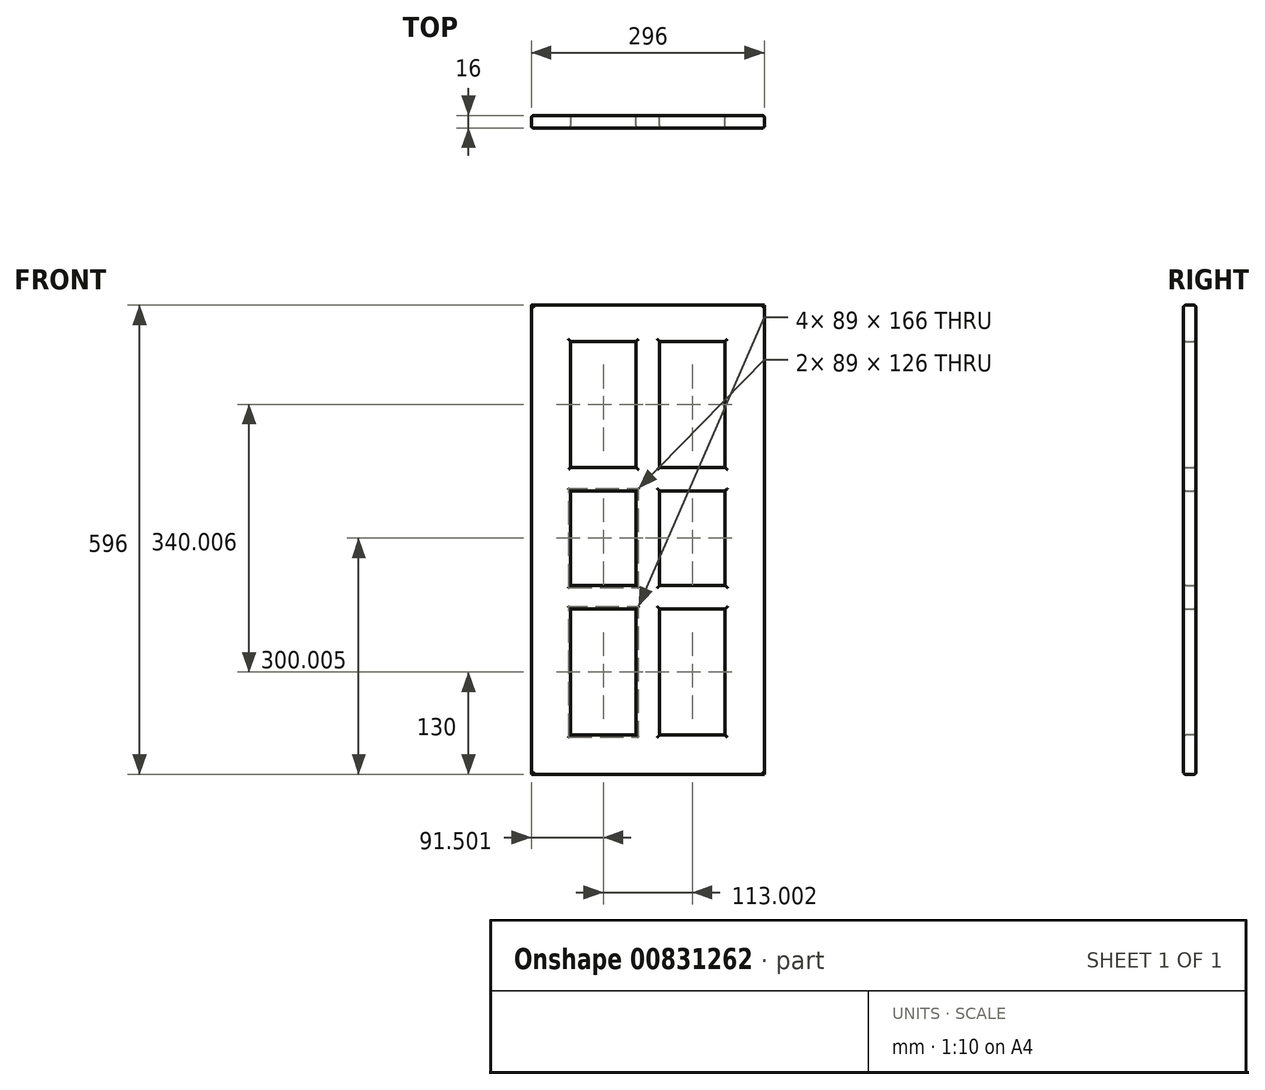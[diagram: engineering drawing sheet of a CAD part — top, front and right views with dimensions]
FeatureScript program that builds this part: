
annotation { "Feature Type Name" : "Feature", "Feature Type Description" : "" }
export const myFeature = defineFeature(function(context is Context, id is Id, definition is map)
    precondition{}
    {
        {
            var Q0;
            Q0=qCreatedBy(makeId("Front.planeOp"),FACE);
            var sketch = newSketch(context, id + "F0", { "sketchPlane" : qUnion([Q0])});
            skLineSegment(sketch, "E0.bottom", {"start": v(0, 0) * mm, "end": v(28.85, 0) * mm});
            skLineSegment(sketch, "E0.top", {"start": v(0, 37.88) * mm, "end": v(28.85, 37.88) * mm});
            skLineSegment(sketch, "E0.left", {"start": v(0, 0) * mm, "end": v(0, 37.88) * mm});
            skLineSegment(sketch, "E0.right", {"start": v(28.85, 0) * mm, "end": v(28.85, 37.88) * mm});
            skSolve(sketch);
        }
        {
            var Q0;
            Q0=makeQuery(id+"F0.imprint","IMPRINT",FACE,{"disambiguationData":[TD([[makeQuery(id+"F0.imprint","IMPRINT",EDGE,{"derivedFrom":sQuery(id+"F0.wireOp",EDGE,"E0.bottom")}),1.0]])]});
            extrude(context, id + "F1", {"entities" : qUnion([Q0]), "depth" : 16 * mm, "offsetDistance" : 25.4 * mm});
        }
        {
            var Q0;
            Q0=makeQuery(id+"F1.opExtrude","SWEPT_FACE",FACE,{"disambiguationData":[OSD([sQuery(id+"F0.wireOp",EDGE,"E0.left")])]});
            extrude(context, id + "F2", {"entities" : qUnion([Q0]), "operationType" : NewBodyOperationType.ADD, "oppositeDirection" : true, "depth" : 296 * mm, "offsetDistance" : 25.4 * mm});
        }
        {
            var Q0;
            {var subQ0=sQuery(id+"F0.wireOp",EDGE,"E0.bottom");Q0=makeQuery(id+"F2.boolean.opBoolean","MERGE",FACE,{"derivedFrom":[makeQuery(id+"F1.opExtrude","SWEPT_FACE",FACE,{"disambiguationData":[OSD([subQ0])]}),makeQuery(id+"F2.opExtrude","SWEPT_FACE",FACE,{"disambiguationData":[OSD([subQ0,sQuery(id+"F0.wireOp",EDGE,"E0.left")])]})]});}
            extrude(context, id + "F3", {"entities" : qUnion([Q0]), "operationType" : NewBodyOperationType.ADD, "oppositeDirection" : true, "depth" : 996 * mm, "offsetDistance" : 25 * mm});
        }
        {
            var Q0;
            {var subQ0=sQuery(id+"F0.wireOp",EDGE,"E0.left");var subQ1=sQuery(id+"F0.wireOp",EDGE,"E0.bottom");Q0=makeQuery(id+"F3.boolean.opBoolean","MERGE",FACE,{"derivedFrom":[makeQuery(id+"F2.boolean.opBoolean","MERGE",FACE,{"derivedFrom":[makeQuery(id+"F1.opExtrude","CAP_FACE",FACE,{"disambiguationData":[OSD([subQ1,sQuery(id+"F0.wireOp",EDGE,"E0.top"),subQ0,sQuery(id+"F0.wireOp",EDGE,"E0.right")])],"isStart":false}),makeQuery(id+"F2.opExtrude","SWEPT_FACE",FACE,{"disambiguationData":[OSD([subQ0]),TDD([makeQuery(id+"F1.opExtrude","CAP_EDGE",EDGE,{"disambiguationData":[OSD([subQ0])],"isStart":false})])]})]}),makeQuery(id+"F3.opExtrude","SWEPT_FACE",FACE,{"disambiguationData":[OSD([subQ1,subQ0]),TDD([makeQuery(id+"F2.boolean.opBoolean","MERGE",EDGE,{"derivedFrom":[makeQuery(id+"F1.opExtrude","CAP_EDGE",EDGE,{"disambiguationData":[OSD([subQ1])],"isStart":false}),makeQuery(id+"F2.opExtrude","SWEPT_EDGE",EDGE,{"disambiguationData":[OSD([subQ1,subQ0]),TDD([makeQuery(id+"F1.opExtrude","CAP_VERTEX",VERTEX,{"disambiguationData":[OSD([subQ1,subQ0])],"isStart":false})])]})]})])]})]});}
            var sketch = newSketch(context, id + "F4", { "sketchPlane" : qUnion([Q0])});
            skLineSegment(sketch, "E1.bottom", {"start": v(48.4, 906.79) * mm, "end": v(248.24, 906.79) * mm});
            skLineSegment(sketch, "E1.top", {"start": v(48.4, 105.66) * mm, "end": v(248.24, 105.66) * mm});
            skLineSegment(sketch, "E1.left", {"start": v(48.4, 906.79) * mm, "end": v(48.4, 105.66) * mm});
            skLineSegment(sketch, "E1.right", {"start": v(248.24, 906.79) * mm, "end": v(248.24, 105.66) * mm});
            skSolve(sketch);
        }
        {
            var Q0;
            Q0=makeQuery(id+"F4.imprint","IMPRINT",FACE,{"disambiguationData":[TD([[makeQuery(id+"F4.imprint","IMPRINT",EDGE,{"derivedFrom":sQuery(id+"F4.wireOp",EDGE,"E1.bottom")}),-1.0]])]});
            extrude(context, id + "F5", {"entities" : qUnion([Q0]), "operationType" : NewBodyOperationType.REMOVE, "oppositeDirection" : true, "depth" : 5 * mm, "offsetDistance" : 25 * mm});
        }
        {
            var Q0;
            Q0=makeQuery(id+"F5.boolean.opBoolean","COPY",FACE,{"derivedFrom":makeQuery(id+"F5.opExtrude","SWEPT_FACE",FACE,{"disambiguationData":[OSD([sQuery(id+"F4.wireOp",EDGE,"E1.bottom")])]})});
            extrude(context, id + "F6", {"entities" : qUnion([Q0]), "operationType" : NewBodyOperationType.REMOVE, "oppositeDirection" : true, "depth" : 39.2 * mm, "offsetDistance" : 25 * mm});
        }
        {
            var Q0;
            {var subQ0=sQuery(id+"F4.wireOp",EDGE,"E1.right");Q0=makeQuery(id+"F6.boolean.opBoolean","MERGE",FACE,{"derivedFrom":[makeQuery(id+"F5.boolean.opBoolean","COPY",FACE,{"derivedFrom":makeQuery(id+"F5.opExtrude","SWEPT_FACE",FACE,{"disambiguationData":[OSD([subQ0])]})}),makeQuery(id+"F6.opExtrude","SWEPT_FACE",FACE,{"disambiguationData":[OSD([sQuery(id+"F4.wireOp",EDGE,"E1.bottom"),subQ0])]})]});}
            extrude(context, id + "F7", {"entities" : qUnion([Q0]), "operationType" : NewBodyOperationType.ADD, "depth" : 2.24 * mm, "offsetDistance" : 25 * mm});
        }
        {
            var Q0;
            Q0=makeQuery(id+"F5.boolean.opBoolean","COPY",FACE,{"derivedFrom":makeQuery(id+"F5.opExtrude","SWEPT_FACE",FACE,{"disambiguationData":[OSD([sQuery(id+"F4.wireOp",EDGE,"E1.top")])]})});
            extrude(context, id + "F8", {"entities" : qUnion([Q0]), "operationType" : NewBodyOperationType.REMOVE, "oppositeDirection" : true, "depth" : 55.66 * mm, "offsetDistance" : 25 * mm});
        }
        {
            var Q0;
            {var subQ0=sQuery(id+"F4.wireOp",EDGE,"E1.left");Q0=makeQuery(id+"F8.boolean.opBoolean","MERGE",FACE,{"derivedFrom":[makeQuery(id+"F6.boolean.opBoolean","MERGE",FACE,{"derivedFrom":[makeQuery(id+"F5.boolean.opBoolean","COPY",FACE,{"derivedFrom":makeQuery(id+"F5.opExtrude","SWEPT_FACE",FACE,{"disambiguationData":[OSD([subQ0])]})}),makeQuery(id+"F6.opExtrude","SWEPT_FACE",FACE,{"disambiguationData":[OSD([sQuery(id+"F4.wireOp",EDGE,"E1.bottom"),subQ0])]})]}),makeQuery(id+"F8.opExtrude","SWEPT_FACE",FACE,{"disambiguationData":[OSD([sQuery(id+"F4.wireOp",EDGE,"E1.top"),subQ0])]})]});}
            extrude(context, id + "F9", {"entities" : qUnion([Q0]), "operationType" : NewBodyOperationType.ADD, "depth" : 1.59 * mm, "offsetDistance" : 25 * mm});
        }
        {
            var Q0;
            {var subQ0=sQuery(id+"F4.wireOp",EDGE,"E1.top");var subQ1=sQuery(id+"F4.wireOp",EDGE,"E1.bottom");Q0=makeQuery(id+"F8.boolean.opBoolean","MERGE",FACE,{"derivedFrom":[makeQuery(id+"F6.boolean.opBoolean","MERGE",FACE,{"derivedFrom":[makeQuery(id+"F5.boolean.opBoolean","COPY",FACE,{"derivedFrom":makeQuery(id+"F5.opExtrude","CAP_FACE",FACE,{"disambiguationData":[OSD([subQ1,subQ0,sQuery(id+"F4.wireOp",EDGE,"E1.left"),sQuery(id+"F4.wireOp",EDGE,"E1.right")])],"isStart":false})}),makeQuery(id+"F6.opExtrude","SWEPT_FACE",FACE,{"disambiguationData":[OSD([subQ1]),TDD([makeQuery(id+"F5.boolean.opBoolean","COPY",EDGE,{"derivedFrom":makeQuery(id+"F5.opExtrude","CAP_EDGE",EDGE,{"disambiguationData":[OSD([subQ1])],"isStart":false})})])]})]}),makeQuery(id+"F8.opExtrude","SWEPT_FACE",FACE,{"disambiguationData":[OSD([subQ0]),TDD([makeQuery(id+"F5.boolean.opBoolean","COPY",EDGE,{"derivedFrom":makeQuery(id+"F5.opExtrude","CAP_EDGE",EDGE,{"disambiguationData":[OSD([subQ0])],"isStart":false})})])]})]});}
            var sketch = newSketch(context, id + "F10", { "sketchPlane" : qUnion([Q0])});
            skLineSegment(sketch, "E2.bottom", {"start": v(127.14, 946) * mm, "end": v(181.91, 946) * mm});
            skLineSegment(sketch, "E2.top", {"start": v(127.14, 50) * mm, "end": v(181.91, 50) * mm});
            skLineSegment(sketch, "E2.left", {"start": v(127.14, 946) * mm, "end": v(127.14, 50) * mm});
            skLineSegment(sketch, "E2.right", {"start": v(181.91, 946) * mm, "end": v(181.91, 50) * mm});
            skSolve(sketch);
        }
        {
            var Q0;
            Q0=makeQuery(id+"F10.imprint","IMPRINT",FACE,{"disambiguationData":[TD([[makeQuery(id+"F10.imprint","IMPRINT",EDGE,{"derivedFrom":sQuery(id+"F10.wireOp",EDGE,"E2.bottom")}),-1.0]])]});
            extrude(context, id + "F11", {"entities" : qUnion([Q0]), "operationType" : NewBodyOperationType.ADD, "depth" : 5 * mm, "offsetDistance" : 25 * mm});
        }
        {
            var Q0;
            Q0=makeQuery(id+"F11.opExtrude","SWEPT_FACE",FACE,{"disambiguationData":[OSD([sQuery(id+"F10.wireOp",EDGE,"E2.left")])]});
            extrude(context, id + "F12", {"entities" : qUnion([Q0]), "operationType" : NewBodyOperationType.REMOVE, "oppositeDirection" : true, "depth" : 5.86 * mm, "offsetDistance" : 25 * mm});
        }
        {
            var Q0;
            Q0=makeQuery(id+"F11.opExtrude","SWEPT_FACE",FACE,{"disambiguationData":[OSD([sQuery(id+"F10.wireOp",EDGE,"E2.right")])]});
            extrude(context, id + "F13", {"entities" : qUnion([Q0]), "operationType" : NewBodyOperationType.REMOVE, "oppositeDirection" : true, "depth" : 18.91 * mm, "offsetDistance" : 25 * mm});
        }
        {
            var Q0;
            {var subQ0=sQuery(id+"F10.wireOp",EDGE,"E2.left");var subQ1=sQuery(id+"F4.wireOp",EDGE,"E1.bottom");var subQ2=sQuery(id+"F4.wireOp",EDGE,"E1.top");var subQ3=sQuery(id+"F4.wireOp",EDGE,"E1.left");Q0=makeQuery(id+"F12.boolean.opBoolean","MERGE",FACE,{"derivedFrom":[makeQuery(id+"F11.boolean.opBoolean","SPLIT",FACE,{"disambiguationData":[TD([makeQuery(id+"F11.opExtrude","SWEPT_FACE",FACE,{"disambiguationData":[OSD([subQ0])]})])],"derivedFrom":makeQuery(id+"F8.boolean.opBoolean","MERGE",FACE,{"derivedFrom":[makeQuery(id+"F6.boolean.opBoolean","MERGE",FACE,{"derivedFrom":[makeQuery(id+"F5.boolean.opBoolean","COPY",FACE,{"derivedFrom":makeQuery(id+"F5.opExtrude","CAP_FACE",FACE,{"disambiguationData":[OSD([subQ1,subQ2,subQ3,sQuery(id+"F4.wireOp",EDGE,"E1.right")])],"isStart":false})}),makeQuery(id+"F6.opExtrude","SWEPT_FACE",FACE,{"disambiguationData":[OSD([subQ1]),TDD([makeQuery(id+"F5.boolean.opBoolean","COPY",EDGE,{"derivedFrom":makeQuery(id+"F5.opExtrude","CAP_EDGE",EDGE,{"disambiguationData":[OSD([subQ1])],"isStart":false})})])]})]}),makeQuery(id+"F8.opExtrude","SWEPT_FACE",FACE,{"disambiguationData":[OSD([subQ2]),TDD([makeQuery(id+"F5.boolean.opBoolean","COPY",EDGE,{"derivedFrom":makeQuery(id+"F5.opExtrude","CAP_EDGE",EDGE,{"disambiguationData":[OSD([subQ2])],"isStart":false})})])]})]})}),makeQuery(id+"F12.opExtrude","SWEPT_FACE",FACE,{"disambiguationData":[OSD([subQ0]),TDD([makeQuery(id+"F11.opExtrude","CAP_EDGE",EDGE,{"disambiguationData":[OSD([subQ0])],"isStart":true})])]})]});}
            var sketch = newSketch(context, id + "F14", { "sketchPlane" : qUnion([Q0])});
            skLineSegment(sketch, "E3.bottom", {"start": v(50, 870.78) * mm, "end": v(133, 870.78) * mm});
            skLineSegment(sketch, "E3.top", {"start": v(50, 835.83) * mm, "end": v(133, 835.83) * mm});
            skLineSegment(sketch, "E3.left", {"start": v(50, 870.78) * mm, "end": v(50, 835.83) * mm});
            skLineSegment(sketch, "E3.right", {"start": v(133, 870.78) * mm, "end": v(133, 835.83) * mm});
            skLineSegment(sketch, "E4.bottom", {"start": v(50, 539.3) * mm, "end": v(133, 539.3) * mm});
            skLineSegment(sketch, "E4.top", {"start": v(50, 484.02) * mm, "end": v(133, 484.02) * mm});
            skLineSegment(sketch, "E4.left", {"start": v(50, 539.3) * mm, "end": v(50, 484.02) * mm});
            skLineSegment(sketch, "E4.right", {"start": v(133, 539.3) * mm, "end": v(133, 484.02) * mm});
            skSolve(sketch);
        }
        {
            var Q0;
            {var subQ0=sQuery(id+"F10.wireOp",EDGE,"E2.right");var subQ1=sQuery(id+"F4.wireOp",EDGE,"E1.top");var subQ2=sQuery(id+"F4.wireOp",EDGE,"E1.right");var subQ3=sQuery(id+"F4.wireOp",EDGE,"E1.bottom");Q0=makeQuery(id+"F13.boolean.opBoolean","MERGE",FACE,{"derivedFrom":[makeQuery(id+"F11.boolean.opBoolean","SPLIT",FACE,{"disambiguationData":[TD([makeQuery(id+"F11.opExtrude","SWEPT_FACE",FACE,{"disambiguationData":[OSD([subQ0])]})])],"derivedFrom":makeQuery(id+"F8.boolean.opBoolean","MERGE",FACE,{"derivedFrom":[makeQuery(id+"F6.boolean.opBoolean","MERGE",FACE,{"derivedFrom":[makeQuery(id+"F5.boolean.opBoolean","COPY",FACE,{"derivedFrom":makeQuery(id+"F5.opExtrude","CAP_FACE",FACE,{"disambiguationData":[OSD([subQ3,subQ1,sQuery(id+"F4.wireOp",EDGE,"E1.left"),subQ2])],"isStart":false})}),makeQuery(id+"F6.opExtrude","SWEPT_FACE",FACE,{"disambiguationData":[OSD([subQ3]),TDD([makeQuery(id+"F5.boolean.opBoolean","COPY",EDGE,{"derivedFrom":makeQuery(id+"F5.opExtrude","CAP_EDGE",EDGE,{"disambiguationData":[OSD([subQ3])],"isStart":false})})])]})]}),makeQuery(id+"F8.opExtrude","SWEPT_FACE",FACE,{"disambiguationData":[OSD([subQ1]),TDD([makeQuery(id+"F5.boolean.opBoolean","COPY",EDGE,{"derivedFrom":makeQuery(id+"F5.opExtrude","CAP_EDGE",EDGE,{"disambiguationData":[OSD([subQ1])],"isStart":false})})])]})]})}),makeQuery(id+"F13.opExtrude","SWEPT_FACE",FACE,{"disambiguationData":[OSD([subQ0]),TDD([makeQuery(id+"F11.opExtrude","CAP_EDGE",EDGE,{"disambiguationData":[OSD([subQ0])],"isStart":true})])]})]});}
            var sketch = newSketch(context, id + "F15", { "sketchPlane" : qUnion([Q0])});
            skLineSegment(sketch, "E5.bottom", {"start": v(163, 876.14) * mm, "end": v(246, 876.14) * mm});
            skLineSegment(sketch, "E5.top", {"start": v(163, 831.26) * mm, "end": v(246, 831.26) * mm});
            skLineSegment(sketch, "E5.left", {"start": v(163, 876.14) * mm, "end": v(163, 831.26) * mm});
            skLineSegment(sketch, "E5.right", {"start": v(246, 876.14) * mm, "end": v(246, 831.26) * mm});
            skLineSegment(sketch, "E6.bottom", {"start": v(163, 602.8) * mm, "end": v(246, 602.8) * mm});
            skLineSegment(sketch, "E6.top", {"start": v(163, 550.28) * mm, "end": v(246, 550.28) * mm});
            skLineSegment(sketch, "E6.left", {"start": v(163, 602.8) * mm, "end": v(163, 550.28) * mm});
            skLineSegment(sketch, "E6.right", {"start": v(246, 602.8) * mm, "end": v(246, 550.28) * mm});
            skSolve(sketch);
        }
        {
            var Q0;
            Q0=makeQuery(id+"F14.imprint","IMPRINT",FACE,{"disambiguationData":[TD([[makeQuery(id+"F14.imprint","IMPRINT",EDGE,{"derivedFrom":sQuery(id+"F14.wireOp",EDGE,"E3.bottom")}),-1.0]])]});
            var Q1;
            Q1=makeQuery(id+"F15.imprint","IMPRINT",FACE,{"disambiguationData":[TD([[makeQuery(id+"F15.imprint","IMPRINT",EDGE,{"derivedFrom":sQuery(id+"F15.wireOp",EDGE,"E5.bottom")}),-1.0]])]});
            var Q2;
            Q2=makeQuery(id+"F15.imprint","IMPRINT",FACE,{"disambiguationData":[TD([[makeQuery(id+"F15.imprint","IMPRINT",EDGE,{"derivedFrom":sQuery(id+"F15.wireOp",EDGE,"E6.bottom")}),-1.0]])]});
            var Q3;
            Q3=makeQuery(id+"F14.imprint","IMPRINT",FACE,{"disambiguationData":[TD([[makeQuery(id+"F14.imprint","IMPRINT",EDGE,{"derivedFrom":sQuery(id+"F14.wireOp",EDGE,"E4.bottom")}),-1.0]])]});
            extrude(context, id + "F16", {"entities" : qUnion([Q0, Q1, Q2, Q3]), "operationType" : NewBodyOperationType.ADD, "depth" : 5 * mm, "offsetDistance" : 25 * mm});
        }
        {
            var Q0;
            Q0=makeQuery(id+"F16.opExtrude","SWEPT_FACE",FACE,{"disambiguationData":[OSD([sQuery(id+"F15.wireOp",EDGE,"E6.top")])]});
            var Q1;
            Q1=makeQuery(id+"F16.opExtrude","SWEPT_FACE",FACE,{"disambiguationData":[OSD([sQuery(id+"F14.wireOp",EDGE,"E4.top")])]});
            extrude(context, id + "F17", {"entities" : qUnion([Q0, Q1]), "operationType" : NewBodyOperationType.ADD, "depth" : 300 * mm, "offsetDistance" : 25 * mm});
        }
        {
            var Q0;
            Q0=makeQuery(id+"F16.opExtrude","SWEPT_FACE",FACE,{"disambiguationData":[OSD([sQuery(id+"F14.wireOp",EDGE,"E4.bottom")])]});
            var Q1;
            Q1=makeQuery(id+"F16.opExtrude","SWEPT_FACE",FACE,{"disambiguationData":[OSD([sQuery(id+"F15.wireOp",EDGE,"E6.bottom")])]});
            extrude(context, id + "F18", {"entities" : qUnion([Q0, Q1]), "operationType" : NewBodyOperationType.REMOVE, "oppositeDirection" : true, "depth" : 300 * mm, "offsetDistance" : 25 * mm});
        }
        {
            var Q0;
            Q0=makeQuery(id+"F16.opExtrude","SWEPT_FACE",FACE,{"disambiguationData":[OSD([sQuery(id+"F14.wireOp",EDGE,"E3.top")])]});
            extrude(context, id + "F19", {"entities" : qUnion([Q0]), "operationType" : NewBodyOperationType.ADD, "depth" : 324.8 * mm, "offsetDistance" : 25 * mm});
        }
        {
            var Q0;
            Q0=makeQuery(id+"F16.opExtrude","SWEPT_FACE",FACE,{"disambiguationData":[OSD([sQuery(id+"F14.wireOp",EDGE,"E3.bottom")])]});
            extrude(context, id + "F20", {"entities" : qUnion([Q0]), "operationType" : NewBodyOperationType.REMOVE, "oppositeDirection" : true, "depth" : 324.8 * mm, "offsetDistance" : 25 * mm});
        }
        {
            var Q0;
            Q0=makeQuery(id+"F18.boolean.opBoolean","COPY",FACE,{"derivedFrom":makeQuery(id+"F18.opExtrude","CAP_FACE",FACE,{"disambiguationData":[OSD([sQuery(id+"F14.wireOp",EDGE,"E4.bottom")])],"isStart":false})});
            extrude(context, id + "F21", {"entities" : qUnion([Q0]), "operationType" : NewBodyOperationType.ADD, "depth" : 250 * mm, "offsetDistance" : 25 * mm});
        }
        {
            var Q0;
            Q0=makeQuery(id+"F17.opExtrude","CAP_FACE",FACE,{"disambiguationData":[OSD([sQuery(id+"F14.wireOp",EDGE,"E4.top")])],"isStart":false});
            extrude(context, id + "F22", {"entities" : qUnion([Q0]), "operationType" : NewBodyOperationType.REMOVE, "oppositeDirection" : true, "depth" : 250 * mm, "offsetDistance" : 25 * mm});
        }
        {
            var Q0;
            Q0=makeQuery(id+"F20.boolean.opBoolean","COPY",FACE,{"derivedFrom":makeQuery(id+"F20.opExtrude","CAP_FACE",FACE,{"disambiguationData":[OSD([sQuery(id+"F14.wireOp",EDGE,"E3.bottom")])],"isStart":false})});
            extrude(context, id + "F23", {"entities" : qUnion([Q0]), "operationType" : NewBodyOperationType.ADD, "depth" : 100 * mm, "offsetDistance" : 25 * mm});
        }
        {
            var Q0;
            Q0=makeQuery(id+"F19.opExtrude","CAP_FACE",FACE,{"disambiguationData":[OSD([sQuery(id+"F14.wireOp",EDGE,"E3.top")])],"isStart":false});
            extrude(context, id + "F24", {"entities" : qUnion([Q0]), "operationType" : NewBodyOperationType.REMOVE, "oppositeDirection" : true, "depth" : 100 * mm, "offsetDistance" : 25 * mm});
        }
        {
            var Q0;
            Q0=makeQuery(id+"F23.opExtrude","CAP_FACE",FACE,{"disambiguationData":[OSD([sQuery(id+"F14.wireOp",EDGE,"E3.bottom")])],"isStart":false});
            extrude(context, id + "F25", {"entities" : qUnion([Q0]), "operationType" : NewBodyOperationType.ADD, "depth" : 50 * mm, "offsetDistance" : 25 * mm});
        }
        {
            var Q0;
            Q0=makeQuery(id+"F24.boolean.opBoolean","COPY",FACE,{"derivedFrom":makeQuery(id+"F24.opExtrude","CAP_FACE",FACE,{"disambiguationData":[OSD([sQuery(id+"F14.wireOp",EDGE,"E3.top")])],"isStart":false})});
            extrude(context, id + "F26", {"entities" : qUnion([Q0]), "operationType" : NewBodyOperationType.REMOVE, "oppositeDirection" : true, "depth" : 50 * mm, "offsetDistance" : 25 * mm});
        }
        {
            var Q0;
            Q0=makeQuery(id+"F22.boolean.opBoolean","COPY",FACE,{"derivedFrom":makeQuery(id+"F22.opExtrude","CAP_FACE",FACE,{"disambiguationData":[OSD([sQuery(id+"F14.wireOp",EDGE,"E4.top")])],"isStart":false})});
            extrude(context, id + "F27", {"entities" : qUnion([Q0]), "operationType" : NewBodyOperationType.ADD, "depth" : 134.02 * mm, "offsetDistance" : 25 * mm});
        }
        {
            var Q0;
            Q0=makeQuery(id+"F27.opExtrude","CAP_FACE",FACE,{"disambiguationData":[OSD([sQuery(id+"F14.wireOp",EDGE,"E4.top")])],"isStart":false});
            extrude(context, id + "F28", {"entities" : qUnion([Q0]), "operationType" : NewBodyOperationType.REMOVE, "oppositeDirection" : true, "depth" : 100 * mm, "offsetDistance" : 25 * mm});
        }
        {
            var Q0;
            Q0=makeQuery(id+"F26.boolean.opBoolean","COPY",FACE,{"derivedFrom":makeQuery(id+"F26.opExtrude","CAP_FACE",FACE,{"disambiguationData":[OSD([sQuery(id+"F14.wireOp",EDGE,"E3.top")])],"isStart":false})});
            extrude(context, id + "F29", {"entities" : qUnion([Q0]), "operationType" : NewBodyOperationType.ADD, "depth" : 100 * mm, "offsetDistance" : 25 * mm});
        }
        {
            var Q0;
            Q0=makeQuery(id+"F25.opExtrude","CAP_FACE",FACE,{"disambiguationData":[OSD([sQuery(id+"F14.wireOp",EDGE,"E3.bottom")])],"isStart":false});
            extrude(context, id + "F30", {"entities" : qUnion([Q0]), "operationType" : NewBodyOperationType.REMOVE, "oppositeDirection" : true, "depth" : 100 * mm, "offsetDistance" : 25 * mm});
        }
        {
            var Q0;
            Q0=makeQuery(id+"F30.boolean.opBoolean","COPY",FACE,{"derivedFrom":makeQuery(id+"F30.opExtrude","CAP_FACE",FACE,{"disambiguationData":[OSD([sQuery(id+"F14.wireOp",EDGE,"E3.bottom")])],"isStart":false})});
            extrude(context, id + "F31", {"entities" : qUnion([Q0]), "operationType" : NewBodyOperationType.ADD, "depth" : 50 * mm, "offsetDistance" : 25 * mm});
        }
        {
            var Q0;
            Q0=makeQuery(id+"F29.opExtrude","CAP_FACE",FACE,{"disambiguationData":[OSD([sQuery(id+"F14.wireOp",EDGE,"E3.top")])],"isStart":false});
            extrude(context, id + "F32", {"entities" : qUnion([Q0]), "operationType" : NewBodyOperationType.REMOVE, "oppositeDirection" : true, "depth" : 54.95 * mm, "offsetDistance" : 25 * mm});
        }
        {
            var Q0;
            Q0=makeQuery(id+"F28.boolean.opBoolean","COPY",FACE,{"derivedFrom":makeQuery(id+"F28.opExtrude","CAP_FACE",FACE,{"disambiguationData":[OSD([sQuery(id+"F14.wireOp",EDGE,"E4.top")])],"isStart":false})});
            extrude(context, id + "F33", {"entities" : qUnion([Q0]), "operationType" : NewBodyOperationType.ADD, "depth" : 50 * mm, "offsetDistance" : 25 * mm});
        }
        {
            var Q0;
            Q0=makeQuery(id+"F21.opExtrude","CAP_FACE",FACE,{"disambiguationData":[OSD([sQuery(id+"F14.wireOp",EDGE,"E4.bottom")])],"isStart":false});
            extrude(context, id + "F34", {"entities" : qUnion([Q0]), "operationType" : NewBodyOperationType.REMOVE, "oppositeDirection" : true, "depth" : 109.3 * mm, "offsetDistance" : 25 * mm});
        }
        {
            var Q0;
            Q0=makeQuery(id+"F16.opExtrude","SWEPT_FACE",FACE,{"disambiguationData":[OSD([sQuery(id+"F15.wireOp",EDGE,"E5.top")])]});
            extrude(context, id + "F35", {"entities" : qUnion([Q0]), "operationType" : NewBodyOperationType.REMOVE, "oppositeDirection" : true, "depth" : 14.88 * mm, "offsetDistance" : 25 * mm});
        }
        {
            var Q0;
            Q0=makeQuery(id+"F35.boolean.opBoolean","COPY",FACE,{"derivedFrom":makeQuery(id+"F35.opExtrude","CAP_FACE",FACE,{"disambiguationData":[OSD([sQuery(id+"F15.wireOp",EDGE,"E5.top")])],"isStart":false})});
            extrude(context, id + "F36", {"entities" : qUnion([Q0]), "operationType" : NewBodyOperationType.ADD, "depth" : 230.15 * mm, "offsetDistance" : 25 * mm});
        }
        {
            var Q0;
            Q0=makeQuery(id+"F16.opExtrude","SWEPT_FACE",FACE,{"disambiguationData":[OSD([sQuery(id+"F15.wireOp",EDGE,"E5.bottom")])]});
            extrude(context, id + "F37", {"entities" : qUnion([Q0]), "operationType" : NewBodyOperationType.REMOVE, "oppositeDirection" : true, "depth" : 230.15 * mm, "offsetDistance" : 25 * mm});
        }
        {
            var Q0;
            Q0=makeQuery(id+"F17.opExtrude","CAP_FACE",FACE,{"disambiguationData":[OSD([sQuery(id+"F15.wireOp",EDGE,"E6.top")])],"isStart":false});
            extrude(context, id + "F38", {"entities" : qUnion([Q0]), "operationType" : NewBodyOperationType.REMOVE, "oppositeDirection" : true, "depth" : 22.52 * mm, "offsetDistance" : 25 * mm});
        }
        {
            var Q0;
            Q0=makeQuery(id+"F18.boolean.opBoolean","COPY",FACE,{"derivedFrom":makeQuery(id+"F18.opExtrude","CAP_FACE",FACE,{"disambiguationData":[OSD([sQuery(id+"F15.wireOp",EDGE,"E6.bottom")])],"isStart":false})});
            extrude(context, id + "F39", {"entities" : qUnion([Q0]), "operationType" : NewBodyOperationType.ADD, "depth" : 77.2 * mm, "offsetDistance" : 25 * mm});
        }
        {
            var Q0;
            Q0=makeQuery(id+"F38.boolean.opBoolean","COPY",FACE,{"derivedFrom":makeQuery(id+"F38.opExtrude","CAP_FACE",FACE,{"disambiguationData":[OSD([sQuery(id+"F15.wireOp",EDGE,"E6.top")])],"isStart":false})});
            extrude(context, id + "F40", {"entities" : qUnion([Q0]), "operationType" : NewBodyOperationType.REMOVE, "oppositeDirection" : true, "depth" : 77.2 * mm, "offsetDistance" : 25 * mm});
        }
        {
            var Q0;
            {var subQ0=sQuery(id+"F14.wireOp",EDGE,"E3.bottom");var subQ1=makeQuery(id+"F16.opExtrude","CAP_EDGE",EDGE,{"disambiguationData":[OSD([subQ0])],"isStart":true});var subQ2=sQuery(id+"F10.wireOp",EDGE,"E2.left");var subQ3=sQuery(id+"F4.wireOp",EDGE,"E1.bottom");var subQ4=sQuery(id+"F4.wireOp",EDGE,"E1.left");var subQ5=sQuery(id+"F4.wireOp",EDGE,"E1.top");var subQ7=makeQuery(id+"F6.boolean.opBoolean","COPY",FACE,{"derivedFrom":makeQuery(id+"F6.opExtrude","CAP_FACE",FACE,{"disambiguationData":[OSD([subQ3])],"isStart":false})});Q0=makeQuery(id+"F30.boolean.opBoolean","MERGE",FACE,{"derivedFrom":[makeQuery(id+"F20.boolean.opBoolean","MERGE",FACE,{"derivedFrom":[makeQuery(id+"F16.boolean.opBoolean","SPLIT",FACE,{"disambiguationData":[TD([subQ7])],"derivedFrom":makeQuery(id+"F12.boolean.opBoolean","MERGE",FACE,{"derivedFrom":[makeQuery(id+"F11.boolean.opBoolean","SPLIT",FACE,{"disambiguationData":[TD([makeQuery(id+"F11.opExtrude","SWEPT_FACE",FACE,{"disambiguationData":[OSD([subQ2])]})])],"derivedFrom":makeQuery(id+"F8.boolean.opBoolean","MERGE",FACE,{"derivedFrom":[makeQuery(id+"F6.boolean.opBoolean","MERGE",FACE,{"derivedFrom":[makeQuery(id+"F5.boolean.opBoolean","COPY",FACE,{"derivedFrom":makeQuery(id+"F5.opExtrude","CAP_FACE",FACE,{"disambiguationData":[OSD([subQ3,subQ5,subQ4,sQuery(id+"F4.wireOp",EDGE,"E1.right")])],"isStart":false})}),makeQuery(id+"F6.opExtrude","SWEPT_FACE",FACE,{"disambiguationData":[OSD([subQ3]),TDD([makeQuery(id+"F5.boolean.opBoolean","COPY",EDGE,{"derivedFrom":makeQuery(id+"F5.opExtrude","CAP_EDGE",EDGE,{"disambiguationData":[OSD([subQ3])],"isStart":false})})])]})]}),makeQuery(id+"F8.opExtrude","SWEPT_FACE",FACE,{"disambiguationData":[OSD([subQ5]),TDD([makeQuery(id+"F5.boolean.opBoolean","COPY",EDGE,{"derivedFrom":makeQuery(id+"F5.opExtrude","CAP_EDGE",EDGE,{"disambiguationData":[OSD([subQ5])],"isStart":false})})])]})]})}),makeQuery(id+"F12.opExtrude","SWEPT_FACE",FACE,{"disambiguationData":[OSD([subQ2]),TDD([makeQuery(id+"F11.opExtrude","CAP_EDGE",EDGE,{"disambiguationData":[OSD([subQ2])],"isStart":true})])]})]})}),makeQuery(id+"F20.opExtrude","SWEPT_FACE",FACE,{"disambiguationData":[OSD([subQ0]),TDD([subQ1])]})]}),makeQuery(id+"F30.opExtrude","SWEPT_FACE",FACE,{"disambiguationData":[OSD([subQ0]),TDD([makeQuery(id+"F25.opExtrude","CAP_EDGE",EDGE,{"disambiguationData":[OSD([subQ0]),TDD([makeQuery(id+"F23.opExtrude","CAP_EDGE",EDGE,{"disambiguationData":[OSD([subQ0]),TDD([makeQuery(id+"F20.boolean.opBoolean","COPY",EDGE,{"derivedFrom":makeQuery(id+"F20.opExtrude","CAP_EDGE",EDGE,{"disambiguationData":[OSD([subQ0]),TDD([subQ1])],"isStart":false})})])],"isStart":false})])],"isStart":false})])]})]});}
            var Q1;
            {var subQ0=sQuery(id+"F15.wireOp",EDGE,"E5.bottom");var subQ1=sQuery(id+"F10.wireOp",EDGE,"E2.right");var subQ2=sQuery(id+"F4.wireOp",EDGE,"E1.bottom");var subQ3=sQuery(id+"F4.wireOp",EDGE,"E1.right");var subQ4=sQuery(id+"F4.wireOp",EDGE,"E1.top");var subQ7=makeQuery(id+"F6.boolean.opBoolean","COPY",FACE,{"derivedFrom":makeQuery(id+"F6.opExtrude","CAP_FACE",FACE,{"disambiguationData":[OSD([subQ2])],"isStart":false})});Q1=makeQuery(id+"F37.boolean.opBoolean","MERGE",FACE,{"derivedFrom":[makeQuery(id+"F16.boolean.opBoolean","SPLIT",FACE,{"disambiguationData":[TD([subQ7])],"derivedFrom":makeQuery(id+"F13.boolean.opBoolean","MERGE",FACE,{"derivedFrom":[makeQuery(id+"F11.boolean.opBoolean","SPLIT",FACE,{"disambiguationData":[TD([makeQuery(id+"F11.opExtrude","SWEPT_FACE",FACE,{"disambiguationData":[OSD([subQ1])]})])],"derivedFrom":makeQuery(id+"F8.boolean.opBoolean","MERGE",FACE,{"derivedFrom":[makeQuery(id+"F6.boolean.opBoolean","MERGE",FACE,{"derivedFrom":[makeQuery(id+"F5.boolean.opBoolean","COPY",FACE,{"derivedFrom":makeQuery(id+"F5.opExtrude","CAP_FACE",FACE,{"disambiguationData":[OSD([subQ2,subQ4,sQuery(id+"F4.wireOp",EDGE,"E1.left"),subQ3])],"isStart":false})}),makeQuery(id+"F6.opExtrude","SWEPT_FACE",FACE,{"disambiguationData":[OSD([subQ2]),TDD([makeQuery(id+"F5.boolean.opBoolean","COPY",EDGE,{"derivedFrom":makeQuery(id+"F5.opExtrude","CAP_EDGE",EDGE,{"disambiguationData":[OSD([subQ2])],"isStart":false})})])]})]}),makeQuery(id+"F8.opExtrude","SWEPT_FACE",FACE,{"disambiguationData":[OSD([subQ4]),TDD([makeQuery(id+"F5.boolean.opBoolean","COPY",EDGE,{"derivedFrom":makeQuery(id+"F5.opExtrude","CAP_EDGE",EDGE,{"disambiguationData":[OSD([subQ4])],"isStart":false})})])]})]})}),makeQuery(id+"F13.opExtrude","SWEPT_FACE",FACE,{"disambiguationData":[OSD([subQ1]),TDD([makeQuery(id+"F11.opExtrude","CAP_EDGE",EDGE,{"disambiguationData":[OSD([subQ1])],"isStart":true})])]})]})}),makeQuery(id+"F37.opExtrude","SWEPT_FACE",FACE,{"disambiguationData":[OSD([subQ0]),TDD([makeQuery(id+"F16.opExtrude","CAP_EDGE",EDGE,{"disambiguationData":[OSD([subQ0])],"isStart":true})])]})]});}
            var Q2;
            {var subQ0=sQuery(id+"F15.wireOp",EDGE,"E5.top");var subQ1=sQuery(id+"F15.wireOp",EDGE,"E6.bottom");var subQ2=sQuery(id+"F10.wireOp",EDGE,"E2.right");var subQ3=sQuery(id+"F4.wireOp",EDGE,"E1.right");var subQ4=sQuery(id+"F4.wireOp",EDGE,"E1.top");var subQ6=sQuery(id+"F4.wireOp",EDGE,"E1.bottom");Q2=makeQuery(id+"F35.boolean.opBoolean","MERGE",FACE,{"derivedFrom":[makeQuery(id+"F18.boolean.opBoolean","MERGE",FACE,{"derivedFrom":[makeQuery(id+"F16.boolean.opBoolean","SPLIT",FACE,{"disambiguationData":[TD([makeQuery(id+"F16.opExtrude","SWEPT_FACE",FACE,{"disambiguationData":[OSD([subQ0])]})])],"derivedFrom":makeQuery(id+"F13.boolean.opBoolean","MERGE",FACE,{"derivedFrom":[makeQuery(id+"F11.boolean.opBoolean","SPLIT",FACE,{"disambiguationData":[TD([makeQuery(id+"F11.opExtrude","SWEPT_FACE",FACE,{"disambiguationData":[OSD([subQ2])]})])],"derivedFrom":makeQuery(id+"F8.boolean.opBoolean","MERGE",FACE,{"derivedFrom":[makeQuery(id+"F6.boolean.opBoolean","MERGE",FACE,{"derivedFrom":[makeQuery(id+"F5.boolean.opBoolean","COPY",FACE,{"derivedFrom":makeQuery(id+"F5.opExtrude","CAP_FACE",FACE,{"disambiguationData":[OSD([subQ6,subQ4,sQuery(id+"F4.wireOp",EDGE,"E1.left"),subQ3])],"isStart":false})}),makeQuery(id+"F6.opExtrude","SWEPT_FACE",FACE,{"disambiguationData":[OSD([subQ6]),TDD([makeQuery(id+"F5.boolean.opBoolean","COPY",EDGE,{"derivedFrom":makeQuery(id+"F5.opExtrude","CAP_EDGE",EDGE,{"disambiguationData":[OSD([subQ6])],"isStart":false})})])]})]}),makeQuery(id+"F8.opExtrude","SWEPT_FACE",FACE,{"disambiguationData":[OSD([subQ4]),TDD([makeQuery(id+"F5.boolean.opBoolean","COPY",EDGE,{"derivedFrom":makeQuery(id+"F5.opExtrude","CAP_EDGE",EDGE,{"disambiguationData":[OSD([subQ4])],"isStart":false})})])]})]})}),makeQuery(id+"F13.opExtrude","SWEPT_FACE",FACE,{"disambiguationData":[OSD([subQ2]),TDD([makeQuery(id+"F11.opExtrude","CAP_EDGE",EDGE,{"disambiguationData":[OSD([subQ2])],"isStart":true})])]})]})}),makeQuery(id+"F18.opExtrude","SWEPT_FACE",FACE,{"disambiguationData":[OSD([subQ1]),TDD([makeQuery(id+"F16.opExtrude","CAP_EDGE",EDGE,{"disambiguationData":[OSD([subQ1])],"isStart":true})])]})]}),makeQuery(id+"F35.opExtrude","SWEPT_FACE",FACE,{"disambiguationData":[OSD([subQ0]),TDD([makeQuery(id+"F16.opExtrude","CAP_EDGE",EDGE,{"disambiguationData":[OSD([subQ0])],"isStart":true})])]})]});}
            var Q3;
            {var subQ0=sQuery(id+"F14.wireOp",EDGE,"E4.bottom");var subQ1=makeQuery(id+"F16.opExtrude","CAP_EDGE",EDGE,{"disambiguationData":[OSD([subQ0])],"isStart":true});var subQ2=sQuery(id+"F14.wireOp",EDGE,"E3.top");var subQ3=makeQuery(id+"F19.opExtrude","CAP_EDGE",EDGE,{"disambiguationData":[OSD([subQ2]),TDD([makeQuery(id+"F16.opExtrude","CAP_EDGE",EDGE,{"disambiguationData":[OSD([subQ2])],"isStart":true})])],"isStart":false});var subQ4=makeQuery(id+"F24.boolean.opBoolean","COPY",EDGE,{"derivedFrom":makeQuery(id+"F24.opExtrude","CAP_EDGE",EDGE,{"disambiguationData":[OSD([subQ2]),TDD([subQ3])],"isStart":false})});var subQ5=sQuery(id+"F4.wireOp",EDGE,"E1.left");var subQ6=sQuery(id+"F4.wireOp",EDGE,"E1.top");var subQ7=sQuery(id+"F4.wireOp",EDGE,"E1.bottom");var subQ9=sQuery(id+"F10.wireOp",EDGE,"E2.left");Q3=makeQuery(id+"F34.boolean.opBoolean","MERGE",FACE,{"derivedFrom":[makeQuery(id+"F32.boolean.opBoolean","MERGE",FACE,{"derivedFrom":[makeQuery(id+"F26.boolean.opBoolean","MERGE",FACE,{"derivedFrom":[makeQuery(id+"F24.boolean.opBoolean","MERGE",FACE,{"derivedFrom":[makeQuery(id+"F18.boolean.opBoolean","MERGE",FACE,{"derivedFrom":[makeQuery(id+"F16.boolean.opBoolean","SPLIT",FACE,{"disambiguationData":[TD([makeQuery(id+"F16.opExtrude","SWEPT_FACE",FACE,{"disambiguationData":[OSD([subQ2])]})])],"derivedFrom":makeQuery(id+"F12.boolean.opBoolean","MERGE",FACE,{"derivedFrom":[makeQuery(id+"F11.boolean.opBoolean","SPLIT",FACE,{"disambiguationData":[TD([makeQuery(id+"F11.opExtrude","SWEPT_FACE",FACE,{"disambiguationData":[OSD([subQ9])]})])],"derivedFrom":makeQuery(id+"F8.boolean.opBoolean","MERGE",FACE,{"derivedFrom":[makeQuery(id+"F6.boolean.opBoolean","MERGE",FACE,{"derivedFrom":[makeQuery(id+"F5.boolean.opBoolean","COPY",FACE,{"derivedFrom":makeQuery(id+"F5.opExtrude","CAP_FACE",FACE,{"disambiguationData":[OSD([subQ7,subQ6,subQ5,sQuery(id+"F4.wireOp",EDGE,"E1.right")])],"isStart":false})}),makeQuery(id+"F6.opExtrude","SWEPT_FACE",FACE,{"disambiguationData":[OSD([subQ7]),TDD([makeQuery(id+"F5.boolean.opBoolean","COPY",EDGE,{"derivedFrom":makeQuery(id+"F5.opExtrude","CAP_EDGE",EDGE,{"disambiguationData":[OSD([subQ7])],"isStart":false})})])]})]}),makeQuery(id+"F8.opExtrude","SWEPT_FACE",FACE,{"disambiguationData":[OSD([subQ6]),TDD([makeQuery(id+"F5.boolean.opBoolean","COPY",EDGE,{"derivedFrom":makeQuery(id+"F5.opExtrude","CAP_EDGE",EDGE,{"disambiguationData":[OSD([subQ6])],"isStart":false})})])]})]})}),makeQuery(id+"F12.opExtrude","SWEPT_FACE",FACE,{"disambiguationData":[OSD([subQ9]),TDD([makeQuery(id+"F11.opExtrude","CAP_EDGE",EDGE,{"disambiguationData":[OSD([subQ9])],"isStart":true})])]})]})}),makeQuery(id+"F18.opExtrude","SWEPT_FACE",FACE,{"disambiguationData":[OSD([subQ0]),TDD([subQ1])]})]}),makeQuery(id+"F24.opExtrude","SWEPT_FACE",FACE,{"disambiguationData":[OSD([subQ2]),TDD([subQ3])]})]}),makeQuery(id+"F26.opExtrude","SWEPT_FACE",FACE,{"disambiguationData":[OSD([subQ2]),TDD([subQ4])]})]}),makeQuery(id+"F32.opExtrude","SWEPT_FACE",FACE,{"disambiguationData":[OSD([subQ2]),TDD([makeQuery(id+"F29.opExtrude","CAP_EDGE",EDGE,{"disambiguationData":[OSD([subQ2]),TDD([makeQuery(id+"F26.boolean.opBoolean","COPY",EDGE,{"derivedFrom":makeQuery(id+"F26.opExtrude","CAP_EDGE",EDGE,{"disambiguationData":[OSD([subQ2]),TDD([subQ4])],"isStart":false})})])],"isStart":false})])]})]}),makeQuery(id+"F34.opExtrude","SWEPT_FACE",FACE,{"disambiguationData":[OSD([subQ0]),TDD([makeQuery(id+"F21.opExtrude","CAP_EDGE",EDGE,{"disambiguationData":[OSD([subQ0]),TDD([makeQuery(id+"F18.boolean.opBoolean","COPY",EDGE,{"derivedFrom":makeQuery(id+"F18.opExtrude","CAP_EDGE",EDGE,{"disambiguationData":[OSD([subQ0]),TDD([subQ1])],"isStart":false})})])],"isStart":false})])]})]});}
            var Q4;
            {var subQ0=sQuery(id+"F14.wireOp",EDGE,"E4.top");var subQ1=makeQuery(id+"F17.opExtrude","CAP_EDGE",EDGE,{"disambiguationData":[OSD([subQ0]),TDD([makeQuery(id+"F16.opExtrude","CAP_EDGE",EDGE,{"disambiguationData":[OSD([subQ0])],"isStart":true})])],"isStart":false});var subQ2=sQuery(id+"F10.wireOp",EDGE,"E2.left");var subQ3=sQuery(id+"F4.wireOp",EDGE,"E1.top");var subQ4=sQuery(id+"F4.wireOp",EDGE,"E1.left");var subQ5=sQuery(id+"F4.wireOp",EDGE,"E1.bottom");var subQ7=makeQuery(id+"F8.boolean.opBoolean","COPY",FACE,{"derivedFrom":makeQuery(id+"F8.opExtrude","CAP_FACE",FACE,{"disambiguationData":[OSD([subQ3])],"isStart":false})});Q4=makeQuery(id+"F28.boolean.opBoolean","MERGE",FACE,{"derivedFrom":[makeQuery(id+"F22.boolean.opBoolean","MERGE",FACE,{"derivedFrom":[makeQuery(id+"F16.boolean.opBoolean","SPLIT",FACE,{"disambiguationData":[TD([subQ7])],"derivedFrom":makeQuery(id+"F12.boolean.opBoolean","MERGE",FACE,{"derivedFrom":[makeQuery(id+"F11.boolean.opBoolean","SPLIT",FACE,{"disambiguationData":[TD([makeQuery(id+"F11.opExtrude","SWEPT_FACE",FACE,{"disambiguationData":[OSD([subQ2])]})])],"derivedFrom":makeQuery(id+"F8.boolean.opBoolean","MERGE",FACE,{"derivedFrom":[makeQuery(id+"F6.boolean.opBoolean","MERGE",FACE,{"derivedFrom":[makeQuery(id+"F5.boolean.opBoolean","COPY",FACE,{"derivedFrom":makeQuery(id+"F5.opExtrude","CAP_FACE",FACE,{"disambiguationData":[OSD([subQ5,subQ3,subQ4,sQuery(id+"F4.wireOp",EDGE,"E1.right")])],"isStart":false})}),makeQuery(id+"F6.opExtrude","SWEPT_FACE",FACE,{"disambiguationData":[OSD([subQ5]),TDD([makeQuery(id+"F5.boolean.opBoolean","COPY",EDGE,{"derivedFrom":makeQuery(id+"F5.opExtrude","CAP_EDGE",EDGE,{"disambiguationData":[OSD([subQ5])],"isStart":false})})])]})]}),makeQuery(id+"F8.opExtrude","SWEPT_FACE",FACE,{"disambiguationData":[OSD([subQ3]),TDD([makeQuery(id+"F5.boolean.opBoolean","COPY",EDGE,{"derivedFrom":makeQuery(id+"F5.opExtrude","CAP_EDGE",EDGE,{"disambiguationData":[OSD([subQ3])],"isStart":false})})])]})]})}),makeQuery(id+"F12.opExtrude","SWEPT_FACE",FACE,{"disambiguationData":[OSD([subQ2]),TDD([makeQuery(id+"F11.opExtrude","CAP_EDGE",EDGE,{"disambiguationData":[OSD([subQ2])],"isStart":true})])]})]})}),makeQuery(id+"F22.opExtrude","SWEPT_FACE",FACE,{"disambiguationData":[OSD([subQ0]),TDD([subQ1])]})]}),makeQuery(id+"F28.opExtrude","SWEPT_FACE",FACE,{"disambiguationData":[OSD([subQ0]),TDD([makeQuery(id+"F27.opExtrude","CAP_EDGE",EDGE,{"disambiguationData":[OSD([subQ0]),TDD([makeQuery(id+"F22.boolean.opBoolean","COPY",EDGE,{"derivedFrom":makeQuery(id+"F22.opExtrude","CAP_EDGE",EDGE,{"disambiguationData":[OSD([subQ0]),TDD([subQ1])],"isStart":false})})])],"isStart":false})])]})]});}
            var Q5;
            {var subQ0=sQuery(id+"F15.wireOp",EDGE,"E6.top");var subQ1=makeQuery(id+"F17.opExtrude","CAP_EDGE",EDGE,{"disambiguationData":[OSD([subQ0]),TDD([makeQuery(id+"F16.opExtrude","CAP_EDGE",EDGE,{"disambiguationData":[OSD([subQ0])],"isStart":true})])],"isStart":false});var subQ2=sQuery(id+"F10.wireOp",EDGE,"E2.right");var subQ3=sQuery(id+"F4.wireOp",EDGE,"E1.top");var subQ4=makeQuery(id+"F8.boolean.opBoolean","COPY",FACE,{"derivedFrom":makeQuery(id+"F8.opExtrude","CAP_FACE",FACE,{"disambiguationData":[OSD([subQ3])],"isStart":false})});var subQ5=sQuery(id+"F4.wireOp",EDGE,"E1.right");var subQ7=sQuery(id+"F4.wireOp",EDGE,"E1.bottom");Q5=makeQuery(id+"F40.boolean.opBoolean","MERGE",FACE,{"derivedFrom":[makeQuery(id+"F38.boolean.opBoolean","MERGE",FACE,{"derivedFrom":[makeQuery(id+"F16.boolean.opBoolean","SPLIT",FACE,{"disambiguationData":[TD([subQ4])],"derivedFrom":makeQuery(id+"F13.boolean.opBoolean","MERGE",FACE,{"derivedFrom":[makeQuery(id+"F11.boolean.opBoolean","SPLIT",FACE,{"disambiguationData":[TD([makeQuery(id+"F11.opExtrude","SWEPT_FACE",FACE,{"disambiguationData":[OSD([subQ2])]})])],"derivedFrom":makeQuery(id+"F8.boolean.opBoolean","MERGE",FACE,{"derivedFrom":[makeQuery(id+"F6.boolean.opBoolean","MERGE",FACE,{"derivedFrom":[makeQuery(id+"F5.boolean.opBoolean","COPY",FACE,{"derivedFrom":makeQuery(id+"F5.opExtrude","CAP_FACE",FACE,{"disambiguationData":[OSD([subQ7,subQ3,sQuery(id+"F4.wireOp",EDGE,"E1.left"),subQ5])],"isStart":false})}),makeQuery(id+"F6.opExtrude","SWEPT_FACE",FACE,{"disambiguationData":[OSD([subQ7]),TDD([makeQuery(id+"F5.boolean.opBoolean","COPY",EDGE,{"derivedFrom":makeQuery(id+"F5.opExtrude","CAP_EDGE",EDGE,{"disambiguationData":[OSD([subQ7])],"isStart":false})})])]})]}),makeQuery(id+"F8.opExtrude","SWEPT_FACE",FACE,{"disambiguationData":[OSD([subQ3]),TDD([makeQuery(id+"F5.boolean.opBoolean","COPY",EDGE,{"derivedFrom":makeQuery(id+"F5.opExtrude","CAP_EDGE",EDGE,{"disambiguationData":[OSD([subQ3])],"isStart":false})})])]})]})}),makeQuery(id+"F13.opExtrude","SWEPT_FACE",FACE,{"disambiguationData":[OSD([subQ2]),TDD([makeQuery(id+"F11.opExtrude","CAP_EDGE",EDGE,{"disambiguationData":[OSD([subQ2])],"isStart":true})])]})]})}),makeQuery(id+"F38.opExtrude","SWEPT_FACE",FACE,{"disambiguationData":[OSD([subQ0]),TDD([subQ1])]})]}),makeQuery(id+"F40.opExtrude","SWEPT_FACE",FACE,{"disambiguationData":[OSD([subQ0]),TDD([makeQuery(id+"F38.boolean.opBoolean","COPY",EDGE,{"derivedFrom":makeQuery(id+"F38.opExtrude","CAP_EDGE",EDGE,{"disambiguationData":[OSD([subQ0]),TDD([subQ1])],"isStart":false})})])]})]});}
            extrude(context, id + "F41", {"entities" : qUnion([Q0, Q1, Q2, Q3, Q4, Q5]), "operationType" : NewBodyOperationType.REMOVE, "oppositeDirection" : true, "depth" : 11 * mm, "offsetDistance" : 25 * mm});
        }
        {
            var Q0;
            {var subQ0=sQuery(id+"F14.wireOp",EDGE,"E4.top");Q0=makeQuery(id+"F41.boolean.opBoolean","MERGE",FACE,{"derivedFrom":[makeQuery(id+"F33.opExtrude","CAP_FACE",FACE,{"disambiguationData":[OSD([subQ0])],"isStart":false}),makeQuery(id+"F41.opExtrude","SWEPT_FACE",FACE,{"disambiguationData":[OSD([subQ0])]})]});}
            var Q1;
            {var subQ0=sQuery(id+"F15.wireOp",EDGE,"E6.top");Q1=makeQuery(id+"F41.boolean.opBoolean","MERGE",FACE,{"derivedFrom":[makeQuery(id+"F40.boolean.opBoolean","COPY",FACE,{"derivedFrom":makeQuery(id+"F40.opExtrude","CAP_FACE",FACE,{"disambiguationData":[OSD([subQ0])],"isStart":false})}),makeQuery(id+"F41.opExtrude","SWEPT_FACE",FACE,{"disambiguationData":[OSD([subQ0])]})]});}
            extrude(context, id + "F42", {"entities" : qUnion([Q0, Q1]), "operationType" : NewBodyOperationType.ADD, "depth" : 100 * mm, "offsetDistance" : 25 * mm});
        }
        {
            var Q0;
            {var subQ0=sQuery(id+"F14.wireOp",EDGE,"E4.bottom");Q0=makeQuery(id+"F41.boolean.opBoolean","MERGE",FACE,{"derivedFrom":[makeQuery(id+"F34.boolean.opBoolean","COPY",FACE,{"derivedFrom":makeQuery(id+"F34.opExtrude","CAP_FACE",FACE,{"disambiguationData":[OSD([subQ0])],"isStart":false})}),makeQuery(id+"F41.opExtrude","SWEPT_FACE",FACE,{"disambiguationData":[OSD([subQ0])]})]});}
            var Q1;
            {var subQ0=sQuery(id+"F15.wireOp",EDGE,"E6.bottom");Q1=makeQuery(id+"F41.boolean.opBoolean","MERGE",FACE,{"derivedFrom":[makeQuery(id+"F39.opExtrude","CAP_FACE",FACE,{"disambiguationData":[OSD([subQ0])],"isStart":false}),makeQuery(id+"F41.opExtrude","SWEPT_FACE",FACE,{"disambiguationData":[OSD([subQ0])]})]});}
            extrude(context, id + "F43", {"entities" : qUnion([Q0, Q1]), "operationType" : NewBodyOperationType.REMOVE, "oppositeDirection" : true, "depth" : 100 * mm, "offsetDistance" : 25 * mm});
        }
        {
            var Q0;
            {var subQ0=sQuery(id+"F14.wireOp",EDGE,"E3.top");Q0=makeQuery(id+"F41.boolean.opBoolean","MERGE",FACE,{"derivedFrom":[makeQuery(id+"F32.boolean.opBoolean","COPY",FACE,{"derivedFrom":makeQuery(id+"F32.opExtrude","CAP_FACE",FACE,{"disambiguationData":[OSD([subQ0])],"isStart":false})}),makeQuery(id+"F41.opExtrude","SWEPT_FACE",FACE,{"disambiguationData":[OSD([subQ0])]})]});}
            var Q1;
            {var subQ0=sQuery(id+"F15.wireOp",EDGE,"E5.top");Q1=makeQuery(id+"F41.boolean.opBoolean","MERGE",FACE,{"derivedFrom":[makeQuery(id+"F36.opExtrude","CAP_FACE",FACE,{"disambiguationData":[OSD([subQ0])],"isStart":false}),makeQuery(id+"F41.opExtrude","SWEPT_FACE",FACE,{"disambiguationData":[OSD([subQ0])]})]});}
            extrude(context, id + "F44", {"entities" : qUnion([Q0, Q1]), "operationType" : NewBodyOperationType.ADD, "depth" : 196 * mm, "offsetDistance" : 25 * mm});
        }
        {
            var Q0;
            {var subQ0=sQuery(id+"F14.wireOp",EDGE,"E3.bottom");Q0=makeQuery(id+"F41.boolean.opBoolean","MERGE",FACE,{"derivedFrom":[makeQuery(id+"F31.opExtrude","CAP_FACE",FACE,{"disambiguationData":[OSD([subQ0])],"isStart":false}),makeQuery(id+"F41.opExtrude","SWEPT_FACE",FACE,{"disambiguationData":[OSD([subQ0])]})]});}
            var Q1;
            {var subQ0=sQuery(id+"F15.wireOp",EDGE,"E5.bottom");Q1=makeQuery(id+"F41.boolean.opBoolean","MERGE",FACE,{"derivedFrom":[makeQuery(id+"F37.boolean.opBoolean","COPY",FACE,{"derivedFrom":makeQuery(id+"F37.opExtrude","CAP_FACE",FACE,{"disambiguationData":[OSD([subQ0])],"isStart":false})}),makeQuery(id+"F41.opExtrude","SWEPT_FACE",FACE,{"disambiguationData":[OSD([subQ0])]})]});}
            extrude(context, id + "F45", {"entities" : qUnion([Q0, Q1]), "operationType" : NewBodyOperationType.REMOVE, "oppositeDirection" : true, "depth" : 196 * mm, "offsetDistance" : 25 * mm});
        }
        {
            var Q0;
            {var subQ0=sQuery(id+"F10.wireOp",EDGE,"E2.left");var subQ1=sQuery(id+"F10.wireOp",EDGE,"E2.bottom");var subQ2=sQuery(id+"F4.wireOp",EDGE,"E1.bottom");Q0=makeQuery(id+"F41.boolean.opBoolean","MERGE",FACE,{"derivedFrom":[makeQuery(id+"F12.boolean.opBoolean","MERGE",FACE,{"derivedFrom":[makeQuery(id+"F11.boolean.opBoolean","SPLIT",FACE,{"disambiguationData":[TD([makeQuery(id+"F11.opExtrude","SWEPT_FACE",FACE,{"disambiguationData":[OSD([subQ0])]})])],"derivedFrom":makeQuery(id+"F6.boolean.opBoolean","COPY",FACE,{"derivedFrom":makeQuery(id+"F6.opExtrude","CAP_FACE",FACE,{"disambiguationData":[OSD([subQ2])],"isStart":false})})}),makeQuery(id+"F12.opExtrude","SWEPT_FACE",FACE,{"disambiguationData":[OSD([subQ2,subQ1,subQ0])]})]}),makeQuery(id+"F41.opExtrude","SWEPT_FACE",FACE,{"disambiguationData":[OSD([subQ2,subQ1,subQ0])]})]});}
            var Q1;
            {var subQ0=sQuery(id+"F10.wireOp",EDGE,"E2.right");var subQ1=sQuery(id+"F10.wireOp",EDGE,"E2.bottom");var subQ2=sQuery(id+"F4.wireOp",EDGE,"E1.bottom");Q1=makeQuery(id+"F41.boolean.opBoolean","MERGE",FACE,{"derivedFrom":[makeQuery(id+"F13.boolean.opBoolean","MERGE",FACE,{"derivedFrom":[makeQuery(id+"F11.boolean.opBoolean","SPLIT",FACE,{"disambiguationData":[TD([makeQuery(id+"F11.opExtrude","SWEPT_FACE",FACE,{"disambiguationData":[OSD([subQ0])]})])],"derivedFrom":makeQuery(id+"F6.boolean.opBoolean","COPY",FACE,{"derivedFrom":makeQuery(id+"F6.opExtrude","CAP_FACE",FACE,{"disambiguationData":[OSD([subQ2])],"isStart":false})})}),makeQuery(id+"F13.opExtrude","SWEPT_FACE",FACE,{"disambiguationData":[OSD([subQ2,subQ1,subQ0])]})]}),makeQuery(id+"F41.opExtrude","SWEPT_FACE",FACE,{"disambiguationData":[OSD([subQ2,subQ1,subQ0])]})]});}
            extrude(context, id + "F46", {"entities" : qUnion([Q0, Q1]), "operationType" : NewBodyOperationType.ADD, "depth" : 296 * mm, "offsetDistance" : 25 * mm});
        }
        {
            var Q0;
            Q0=makeQuery(id+"F3.opExtrude","CAP_FACE",FACE,{"disambiguationData":[OSD([sQuery(id+"F0.wireOp",EDGE,"E0.bottom"),sQuery(id+"F0.wireOp",EDGE,"E0.left")])],"isStart":false});
            extrude(context, id + "F47", {"entities" : qUnion([Q0]), "operationType" : NewBodyOperationType.REMOVE, "oppositeDirection" : true, "depth" : 296 * mm, "offsetDistance" : 25 * mm});
        }
        {
            var Q0;
            Q0=makeQuery(id+"F46.opExtrude","CAP_FACE",FACE,{"disambiguationData":[OSD([sQuery(id+"F4.wireOp",EDGE,"E1.bottom"),sQuery(id+"F10.wireOp",EDGE,"E2.bottom"),sQuery(id+"F10.wireOp",EDGE,"E2.right")])],"isStart":false});
            var Q1;
            Q1=makeQuery(id+"F46.opExtrude","CAP_FACE",FACE,{"disambiguationData":[OSD([sQuery(id+"F4.wireOp",EDGE,"E1.bottom"),sQuery(id+"F10.wireOp",EDGE,"E2.bottom"),sQuery(id+"F10.wireOp",EDGE,"E2.left")])],"isStart":false});
            extrude(context, id + "F48", {"entities" : qUnion([Q0, Q1]), "operationType" : NewBodyOperationType.ADD, "depth" : 100 * mm, "offsetDistance" : 25 * mm});
        }
        {
            var Q0;
            Q0=makeQuery(id+"F47.boolean.opBoolean","COPY",FACE,{"derivedFrom":makeQuery(id+"F47.opExtrude","CAP_FACE",FACE,{"disambiguationData":[OSD([sQuery(id+"F0.wireOp",EDGE,"E0.bottom"),sQuery(id+"F0.wireOp",EDGE,"E0.left")])],"isStart":false})});
            extrude(context, id + "F49", {"entities" : qUnion([Q0]), "operationType" : NewBodyOperationType.REMOVE, "oppositeDirection" : true, "depth" : 104 * mm, "offsetDistance" : 25 * mm});
        }
        {
            var Q0;
            Q0=makeQuery(id+"F42.opExtrude","CAP_FACE",FACE,{"disambiguationData":[OSD([sQuery(id+"F14.wireOp",EDGE,"E4.top")])],"isStart":false});
            extrude(context, id + "F50", {"entities" : qUnion([Q0]), "operationType" : NewBodyOperationType.ADD, "depth" : 20 * mm, "offsetDistance" : 25 * mm});
        }
        {
            var Q0;
            Q0=makeQuery(id+"F42.opExtrude","CAP_FACE",FACE,{"disambiguationData":[OSD([sQuery(id+"F15.wireOp",EDGE,"E6.top")])],"isStart":false});
            extrude(context, id + "F51", {"entities" : qUnion([Q0]), "operationType" : NewBodyOperationType.ADD, "depth" : 20 * mm, "offsetDistance" : 25 * mm});
        }
        {
            var Q0;
            Q0=makeQuery(id+"F43.boolean.opBoolean","COPY",FACE,{"derivedFrom":makeQuery(id+"F43.opExtrude","CAP_FACE",FACE,{"disambiguationData":[OSD([sQuery(id+"F14.wireOp",EDGE,"E4.bottom")])],"isStart":false})});
            var Q1;
            Q1=makeQuery(id+"F43.boolean.opBoolean","COPY",FACE,{"derivedFrom":makeQuery(id+"F43.opExtrude","CAP_FACE",FACE,{"disambiguationData":[OSD([sQuery(id+"F15.wireOp",EDGE,"E6.bottom")])],"isStart":false})});
            extrude(context, id + "F52", {"entities" : qUnion([Q0, Q1]), "operationType" : NewBodyOperationType.REMOVE, "oppositeDirection" : true, "depth" : 20 * mm, "offsetDistance" : 25 * mm});
        }
        {
            var Q0;
            Q0=makeQuery(id+"F44.opExtrude","CAP_FACE",FACE,{"disambiguationData":[OSD([sQuery(id+"F15.wireOp",EDGE,"E5.top")])],"isStart":false});
            var Q1;
            Q1=makeQuery(id+"F44.opExtrude","CAP_FACE",FACE,{"disambiguationData":[OSD([sQuery(id+"F14.wireOp",EDGE,"E3.top")])],"isStart":false});
            extrude(context, id + "F53", {"entities" : qUnion([Q0, Q1]), "operationType" : NewBodyOperationType.ADD, "depth" : 80 * mm, "offsetDistance" : 25 * mm});
        }
        {
            var Q0;
            Q0=makeQuery(id+"F45.boolean.opBoolean","COPY",FACE,{"derivedFrom":makeQuery(id+"F45.opExtrude","CAP_FACE",FACE,{"disambiguationData":[OSD([sQuery(id+"F14.wireOp",EDGE,"E3.bottom")])],"isStart":false})});
            var Q1;
            Q1=makeQuery(id+"F45.boolean.opBoolean","COPY",FACE,{"derivedFrom":makeQuery(id+"F45.opExtrude","CAP_FACE",FACE,{"disambiguationData":[OSD([sQuery(id+"F15.wireOp",EDGE,"E5.bottom")])],"isStart":false})});
            extrude(context, id + "F54", {"entities" : qUnion([Q0, Q1]), "operationType" : NewBodyOperationType.REMOVE, "oppositeDirection" : true, "depth" : 80 * mm, "offsetDistance" : 25 * mm});
        }
        {
            var Q0;
            Q0=makeQuery(id+"F54.boolean.opBoolean","COPY",FACE,{"derivedFrom":makeQuery(id+"F54.opExtrude","CAP_FACE",FACE,{"disambiguationData":[OSD([sQuery(id+"F15.wireOp",EDGE,"E5.bottom")])],"isStart":false})});
            var Q1;
            Q1=makeQuery(id+"F54.boolean.opBoolean","COPY",FACE,{"derivedFrom":makeQuery(id+"F54.opExtrude","CAP_FACE",FACE,{"disambiguationData":[OSD([sQuery(id+"F14.wireOp",EDGE,"E3.bottom")])],"isStart":false})});
            extrude(context, id + "F55", {"entities" : qUnion([Q0, Q1]), "operationType" : NewBodyOperationType.ADD, "depth" : 20 * mm, "offsetDistance" : 25 * mm});
        }
        {
            var Q0;
            Q0=makeQuery(id+"F53.opExtrude","CAP_FACE",FACE,{"disambiguationData":[OSD([sQuery(id+"F14.wireOp",EDGE,"E3.top")])],"isStart":false});
            var Q1;
            Q1=makeQuery(id+"F53.opExtrude","CAP_FACE",FACE,{"disambiguationData":[OSD([sQuery(id+"F15.wireOp",EDGE,"E5.top")])],"isStart":false});
            extrude(context, id + "F56", {"entities" : qUnion([Q0, Q1]), "operationType" : NewBodyOperationType.REMOVE, "oppositeDirection" : true, "depth" : 20 * mm, "offsetDistance" : 25 * mm});
        }
        {
            var Q0;
            Q0=makeQuery(id+"F51.opExtrude","CAP_FACE",FACE,{"disambiguationData":[OSD([sQuery(id+"F15.wireOp",EDGE,"E6.top")])],"isStart":false});
            var Q1;
            Q1=makeQuery(id+"F50.opExtrude","CAP_FACE",FACE,{"disambiguationData":[OSD([sQuery(id+"F14.wireOp",EDGE,"E4.top")])],"isStart":false});
            extrude(context, id + "F57", {"entities" : qUnion([Q0, Q1]), "operationType" : NewBodyOperationType.ADD, "depth" : 20 * mm, "offsetDistance" : 25 * mm});
        }
        {
            var Q0;
            Q0=makeQuery(id+"F52.boolean.opBoolean","COPY",FACE,{"derivedFrom":makeQuery(id+"F52.opExtrude","CAP_FACE",FACE,{"disambiguationData":[OSD([sQuery(id+"F15.wireOp",EDGE,"E6.bottom")])],"isStart":false})});
            var Q1;
            Q1=makeQuery(id+"F52.boolean.opBoolean","COPY",FACE,{"derivedFrom":makeQuery(id+"F52.opExtrude","CAP_FACE",FACE,{"disambiguationData":[OSD([sQuery(id+"F14.wireOp",EDGE,"E4.bottom")])],"isStart":false})});
            extrude(context, id + "F58", {"entities" : qUnion([Q0, Q1]), "operationType" : NewBodyOperationType.REMOVE, "oppositeDirection" : true, "depth" : 20 * mm, "offsetDistance" : 25 * mm});
        }
        {
            var Q0;
            {var subQ0=sQuery(id+"F15.wireOp",EDGE,"E6.top");var subQ1=makeQuery(id+"F16.opExtrude","CAP_EDGE",EDGE,{"disambiguationData":[OSD([subQ0])],"isStart":false});var subQ2=makeQuery(id+"F40.boolean.opBoolean","COPY",EDGE,{"derivedFrom":makeQuery(id+"F40.opExtrude","CAP_EDGE",EDGE,{"disambiguationData":[OSD([subQ0]),TDD([makeQuery(id+"F38.boolean.opBoolean","COPY",EDGE,{"derivedFrom":makeQuery(id+"F38.opExtrude","CAP_EDGE",EDGE,{"disambiguationData":[OSD([subQ0]),TDD([makeQuery(id+"F17.opExtrude","CAP_EDGE",EDGE,{"disambiguationData":[OSD([subQ0]),TDD([subQ1])],"isStart":false})])],"isStart":false})})])],"isStart":false})});var subQ3=makeQuery(id+"F42.opExtrude","CAP_EDGE",EDGE,{"disambiguationData":[OSD([subQ0]),TDD([subQ2])],"isStart":false});var subQ4=sQuery(id+"F14.wireOp",EDGE,"E4.top");var subQ5=makeQuery(id+"F16.opExtrude","CAP_EDGE",EDGE,{"disambiguationData":[OSD([subQ4])],"isStart":false});var subQ6=makeQuery(id+"F22.boolean.opBoolean","COPY",EDGE,{"derivedFrom":makeQuery(id+"F22.opExtrude","CAP_EDGE",EDGE,{"disambiguationData":[OSD([subQ4]),TDD([makeQuery(id+"F17.opExtrude","CAP_EDGE",EDGE,{"disambiguationData":[OSD([subQ4]),TDD([subQ5])],"isStart":false})])],"isStart":false})});var subQ7=makeQuery(id+"F28.boolean.opBoolean","COPY",EDGE,{"derivedFrom":makeQuery(id+"F28.opExtrude","CAP_EDGE",EDGE,{"disambiguationData":[OSD([subQ4]),TDD([makeQuery(id+"F27.opExtrude","CAP_EDGE",EDGE,{"disambiguationData":[OSD([subQ4]),TDD([subQ6])],"isStart":false})])],"isStart":false})});var subQ8=makeQuery(id+"F33.opExtrude","CAP_EDGE",EDGE,{"disambiguationData":[OSD([subQ4]),TDD([subQ7])],"isStart":false});var subQ9=makeQuery(id+"F42.opExtrude","CAP_EDGE",EDGE,{"disambiguationData":[OSD([subQ4]),TDD([subQ8])],"isStart":false});var subQ10=sQuery(id+"F15.wireOp",EDGE,"E5.bottom");var subQ11=sQuery(id+"F14.wireOp",EDGE,"E3.bottom");var subQ12=makeQuery(id+"F20.boolean.opBoolean","COPY",EDGE,{"derivedFrom":makeQuery(id+"F20.opExtrude","CAP_EDGE",EDGE,{"disambiguationData":[OSD([subQ11]),TDD([makeQuery(id+"F16.opExtrude","CAP_EDGE",EDGE,{"disambiguationData":[OSD([subQ11])],"isStart":false})])],"isStart":false})});var subQ13=makeQuery(id+"F23.opExtrude","CAP_EDGE",EDGE,{"disambiguationData":[OSD([subQ11]),TDD([subQ12])],"isStart":false});var subQ14=makeQuery(id+"F30.boolean.opBoolean","COPY",EDGE,{"derivedFrom":makeQuery(id+"F30.opExtrude","CAP_EDGE",EDGE,{"disambiguationData":[OSD([subQ11]),TDD([makeQuery(id+"F25.opExtrude","CAP_EDGE",EDGE,{"disambiguationData":[OSD([subQ11]),TDD([subQ13])],"isStart":false})])],"isStart":false})});var subQ15=sQuery(id+"F15.wireOp",EDGE,"E5.top");var subQ16=makeQuery(id+"F35.boolean.opBoolean","COPY",EDGE,{"derivedFrom":makeQuery(id+"F35.opExtrude","CAP_EDGE",EDGE,{"disambiguationData":[OSD([subQ15]),TDD([makeQuery(id+"F16.opExtrude","CAP_EDGE",EDGE,{"disambiguationData":[OSD([subQ15])],"isStart":false})])],"isStart":false})});var subQ17=makeQuery(id+"F36.opExtrude","CAP_EDGE",EDGE,{"disambiguationData":[OSD([subQ15]),TDD([subQ16])],"isStart":false});var subQ18=sQuery(id+"F14.wireOp",EDGE,"E3.top");var subQ19=makeQuery(id+"F16.opExtrude","CAP_EDGE",EDGE,{"disambiguationData":[OSD([subQ18])],"isStart":false});var subQ20=makeQuery(id+"F26.boolean.opBoolean","COPY",EDGE,{"derivedFrom":makeQuery(id+"F26.opExtrude","CAP_EDGE",EDGE,{"disambiguationData":[OSD([subQ18]),TDD([makeQuery(id+"F24.boolean.opBoolean","COPY",EDGE,{"derivedFrom":makeQuery(id+"F24.opExtrude","CAP_EDGE",EDGE,{"disambiguationData":[OSD([subQ18]),TDD([makeQuery(id+"F19.opExtrude","CAP_EDGE",EDGE,{"disambiguationData":[OSD([subQ18]),TDD([subQ19])],"isStart":false})])],"isStart":false})})])],"isStart":false})});var subQ21=makeQuery(id+"F32.boolean.opBoolean","COPY",EDGE,{"derivedFrom":makeQuery(id+"F32.opExtrude","CAP_EDGE",EDGE,{"disambiguationData":[OSD([subQ18]),TDD([makeQuery(id+"F29.opExtrude","CAP_EDGE",EDGE,{"disambiguationData":[OSD([subQ18]),TDD([subQ20])],"isStart":false})])],"isStart":false})});var subQ22=sQuery(id+"F10.wireOp",EDGE,"E2.right");var subQ23=sQuery(id+"F10.wireOp",EDGE,"E2.bottom");var subQ24=sQuery(id+"F4.wireOp",EDGE,"E1.bottom");var subQ26=sQuery(id+"F0.wireOp",EDGE,"E0.left");var subQ27=sQuery(id+"F0.wireOp",EDGE,"E0.bottom");var subQ28=makeQuery(id+"F3.opExtrude","SWEPT_FACE",FACE,{"disambiguationData":[OSD([subQ27,subQ26]),TDD([makeQuery(id+"F2.boolean.opBoolean","MERGE",EDGE,{"derivedFrom":[makeQuery(id+"F1.opExtrude","CAP_EDGE",EDGE,{"disambiguationData":[OSD([subQ27])],"isStart":false}),makeQuery(id+"F2.opExtrude","SWEPT_EDGE",EDGE,{"disambiguationData":[OSD([subQ27,subQ26]),TDD([makeQuery(id+"F1.opExtrude","CAP_VERTEX",VERTEX,{"disambiguationData":[OSD([subQ27,subQ26])],"isStart":false})])]})]})])]});var subQ29=makeQuery(id+"F2.opExtrude","SWEPT_FACE",FACE,{"disambiguationData":[OSD([subQ26]),TDD([makeQuery(id+"F1.opExtrude","CAP_EDGE",EDGE,{"disambiguationData":[OSD([subQ26])],"isStart":false})])]});var subQ30=makeQuery(id+"F1.opExtrude","CAP_FACE",FACE,{"disambiguationData":[OSD([subQ27,sQuery(id+"F0.wireOp",EDGE,"E0.top"),subQ26,sQuery(id+"F0.wireOp",EDGE,"E0.right")])],"isStart":false});var subQ31=sQuery(id+"F4.wireOp",EDGE,"E1.right");var subQ32=makeQuery(id+"F7.opExtrude","SWEPT_FACE",FACE,{"disambiguationData":[OSD([subQ24,subQ31]),TDD([makeQuery(id+"F6.boolean.opBoolean","MERGE",EDGE,{"derivedFrom":[makeQuery(id+"F5.boolean.opBoolean","COPY",EDGE,{"derivedFrom":makeQuery(id+"F5.opExtrude","CAP_EDGE",EDGE,{"disambiguationData":[OSD([subQ31])],"isStart":true})}),makeQuery(id+"F6.opExtrude","SWEPT_EDGE",EDGE,{"disambiguationData":[OSD([subQ24,subQ31]),TDD([makeQuery(id+"F5.boolean.opBoolean","COPY",VERTEX,{"derivedFrom":makeQuery(id+"F5.opExtrude","CAP_VERTEX",VERTEX,{"disambiguationData":[OSD([subQ24,subQ31])],"isStart":true})})])]})]})])]});var subQ33=sQuery(id+"F10.wireOp",EDGE,"E2.left");var subQ34=makeQuery(id+"F11.opExtrude","CAP_FACE",FACE,{"disambiguationData":[OSD([subQ23,sQuery(id+"F10.wireOp",EDGE,"E2.top"),subQ33,subQ22])],"isStart":false});var subQ35=sQuery(id+"F4.wireOp",EDGE,"E1.top");var subQ36=sQuery(id+"F4.wireOp",EDGE,"E1.left");var subQ37=makeQuery(id+"F9.opExtrude","SWEPT_FACE",FACE,{"disambiguationData":[OSD([subQ24,subQ35,subQ36]),TDD([makeQuery(id+"F8.boolean.opBoolean","MERGE",EDGE,{"derivedFrom":[makeQuery(id+"F6.boolean.opBoolean","MERGE",EDGE,{"derivedFrom":[makeQuery(id+"F5.boolean.opBoolean","COPY",EDGE,{"derivedFrom":makeQuery(id+"F5.opExtrude","CAP_EDGE",EDGE,{"disambiguationData":[OSD([subQ36])],"isStart":true})}),makeQuery(id+"F6.opExtrude","SWEPT_EDGE",EDGE,{"disambiguationData":[OSD([subQ24,subQ36]),TDD([makeQuery(id+"F5.boolean.opBoolean","COPY",VERTEX,{"derivedFrom":makeQuery(id+"F5.opExtrude","CAP_VERTEX",VERTEX,{"disambiguationData":[OSD([subQ24,subQ36])],"isStart":true})})])]})]}),makeQuery(id+"F8.opExtrude","SWEPT_EDGE",EDGE,{"disambiguationData":[OSD([subQ35,subQ36]),TDD([makeQuery(id+"F5.boolean.opBoolean","COPY",VERTEX,{"derivedFrom":makeQuery(id+"F5.opExtrude","CAP_VERTEX",VERTEX,{"disambiguationData":[OSD([subQ35,subQ36])],"isStart":true})})])]})]})])]});var subQ38=makeQuery(id+"F6.boolean.opBoolean","COPY",EDGE,{"derivedFrom":makeQuery(id+"F6.opExtrude","CAP_EDGE",EDGE,{"disambiguationData":[OSD([subQ24]),TDD([makeQuery(id+"F5.boolean.opBoolean","COPY",EDGE,{"derivedFrom":makeQuery(id+"F5.opExtrude","CAP_EDGE",EDGE,{"disambiguationData":[OSD([subQ24])],"isStart":true})})])],"isStart":false})});var subQ39=makeQuery(id+"F13.boolean.opBoolean","MERGE",EDGE,{"derivedFrom":[makeQuery(id+"F11.boolean.opBoolean","SPLIT",EDGE,{"disambiguationData":[TD([makeQuery(id+"F11.opExtrude","SWEPT_FACE",FACE,{"disambiguationData":[OSD([subQ22])]})])],"derivedFrom":subQ38}),makeQuery(id+"F13.opExtrude","SWEPT_EDGE",EDGE,{"disambiguationData":[OSD([subQ24,subQ23,subQ22]),TDD([makeQuery(id+"F11.opExtrude","CAP_VERTEX",VERTEX,{"disambiguationData":[OSD([subQ24,subQ23,subQ22])],"isStart":false})])]})]});var subQ40=makeQuery(id+"F12.boolean.opBoolean","MERGE",EDGE,{"derivedFrom":[makeQuery(id+"F11.boolean.opBoolean","SPLIT",EDGE,{"disambiguationData":[TD([makeQuery(id+"F11.opExtrude","SWEPT_FACE",FACE,{"disambiguationData":[OSD([subQ33])]})])],"derivedFrom":subQ38}),makeQuery(id+"F12.opExtrude","SWEPT_EDGE",EDGE,{"disambiguationData":[OSD([subQ24,subQ23,subQ33]),TDD([makeQuery(id+"F11.opExtrude","CAP_VERTEX",VERTEX,{"disambiguationData":[OSD([subQ24,subQ23,subQ33])],"isStart":false})])]})]});var subQ41=sQuery(id+"F15.wireOp",EDGE,"E6.bottom");var subQ42=sQuery(id+"F14.wireOp",EDGE,"E4.bottom");Q0=makeQuery(id+"F57.boolean.opBoolean","MERGE",FACE,{"derivedFrom":[makeQuery(id+"F55.boolean.opBoolean","MERGE",FACE,{"derivedFrom":[makeQuery(id+"F53.boolean.opBoolean","MERGE",FACE,{"derivedFrom":[makeQuery(id+"F51.boolean.opBoolean","MERGE",FACE,{"derivedFrom":[makeQuery(id+"F50.boolean.opBoolean","MERGE",FACE,{"derivedFrom":[makeQuery(id+"F48.boolean.opBoolean","MERGE",FACE,{"derivedFrom":[makeQuery(id+"F46.boolean.opBoolean","MERGE",FACE,{"derivedFrom":[makeQuery(id+"F44.boolean.opBoolean","MERGE",FACE,{"derivedFrom":[makeQuery(id+"F42.boolean.opBoolean","MERGE",FACE,{"derivedFrom":[makeQuery(id+"F39.boolean.opBoolean","MERGE",FACE,{"derivedFrom":[makeQuery(id+"F36.boolean.opBoolean","MERGE",FACE,{"derivedFrom":[makeQuery(id+"F33.boolean.opBoolean","MERGE",FACE,{"derivedFrom":[makeQuery(id+"F31.boolean.opBoolean","MERGE",FACE,{"derivedFrom":[makeQuery(id+"F29.boolean.opBoolean","MERGE",FACE,{"derivedFrom":[makeQuery(id+"F27.boolean.opBoolean","MERGE",FACE,{"derivedFrom":[makeQuery(id+"F25.boolean.opBoolean","MERGE",FACE,{"derivedFrom":[makeQuery(id+"F23.boolean.opBoolean","MERGE",FACE,{"derivedFrom":[makeQuery(id+"F21.boolean.opBoolean","MERGE",FACE,{"derivedFrom":[makeQuery(id+"F19.boolean.opBoolean","MERGE",FACE,{"derivedFrom":[makeQuery(id+"F17.boolean.opBoolean","MERGE",FACE,{"derivedFrom":[makeQuery(id+"F16.boolean.opBoolean","MERGE",FACE,{"derivedFrom":[makeQuery(id+"F11.boolean.opBoolean","MERGE",FACE,{"derivedFrom":[makeQuery(id+"F9.boolean.opBoolean","MERGE",FACE,{"derivedFrom":[makeQuery(id+"F7.boolean.opBoolean","MERGE",FACE,{"derivedFrom":[makeQuery(id+"F3.boolean.opBoolean","MERGE",FACE,{"derivedFrom":[makeQuery(id+"F2.boolean.opBoolean","MERGE",FACE,{"derivedFrom":[subQ30,subQ29]}),subQ28]}),subQ32]}),subQ37]}),subQ34]}),makeQuery(id+"F16.opExtrude","CAP_FACE",FACE,{"disambiguationData":[OSD([subQ11,subQ18,sQuery(id+"F14.wireOp",EDGE,"E3.left"),sQuery(id+"F14.wireOp",EDGE,"E3.right")])],"isStart":false}),makeQuery(id+"F16.opExtrude","CAP_FACE",FACE,{"disambiguationData":[OSD([subQ42,subQ4,sQuery(id+"F14.wireOp",EDGE,"E4.left"),sQuery(id+"F14.wireOp",EDGE,"E4.right")])],"isStart":false}),makeQuery(id+"F16.opExtrude","CAP_FACE",FACE,{"disambiguationData":[OSD([subQ10,subQ15,sQuery(id+"F15.wireOp",EDGE,"E5.left"),sQuery(id+"F15.wireOp",EDGE,"E5.right")])],"isStart":false}),makeQuery(id+"F16.opExtrude","CAP_FACE",FACE,{"disambiguationData":[OSD([subQ41,subQ0,sQuery(id+"F15.wireOp",EDGE,"E6.left"),sQuery(id+"F15.wireOp",EDGE,"E6.right")])],"isStart":false})]}),makeQuery(id+"F17.opExtrude","SWEPT_FACE",FACE,{"disambiguationData":[OSD([subQ4]),TDD([subQ5])]}),makeQuery(id+"F17.opExtrude","SWEPT_FACE",FACE,{"disambiguationData":[OSD([subQ0]),TDD([subQ1])]})]}),makeQuery(id+"F19.opExtrude","SWEPT_FACE",FACE,{"disambiguationData":[OSD([subQ18]),TDD([subQ19])]})]}),makeQuery(id+"F21.opExtrude","SWEPT_FACE",FACE,{"disambiguationData":[OSD([subQ42]),TDD([makeQuery(id+"F18.boolean.opBoolean","COPY",EDGE,{"derivedFrom":makeQuery(id+"F18.opExtrude","CAP_EDGE",EDGE,{"disambiguationData":[OSD([subQ42]),TDD([makeQuery(id+"F16.opExtrude","CAP_EDGE",EDGE,{"disambiguationData":[OSD([subQ42])],"isStart":false})])],"isStart":false})})])]})]}),makeQuery(id+"F23.opExtrude","SWEPT_FACE",FACE,{"disambiguationData":[OSD([subQ11]),TDD([subQ12])]})]}),makeQuery(id+"F25.opExtrude","SWEPT_FACE",FACE,{"disambiguationData":[OSD([subQ11]),TDD([subQ13])]})]}),makeQuery(id+"F27.opExtrude","SWEPT_FACE",FACE,{"disambiguationData":[OSD([subQ4]),TDD([subQ6])]})]}),makeQuery(id+"F29.opExtrude","SWEPT_FACE",FACE,{"disambiguationData":[OSD([subQ18]),TDD([subQ20])]})]}),makeQuery(id+"F31.opExtrude","SWEPT_FACE",FACE,{"disambiguationData":[OSD([subQ11]),TDD([subQ14])]})]}),makeQuery(id+"F33.opExtrude","SWEPT_FACE",FACE,{"disambiguationData":[OSD([subQ4]),TDD([subQ7])]})]}),makeQuery(id+"F36.opExtrude","SWEPT_FACE",FACE,{"disambiguationData":[OSD([subQ15]),TDD([subQ16])]})]}),makeQuery(id+"F39.opExtrude","SWEPT_FACE",FACE,{"disambiguationData":[OSD([subQ41]),TDD([makeQuery(id+"F18.boolean.opBoolean","COPY",EDGE,{"derivedFrom":makeQuery(id+"F18.opExtrude","CAP_EDGE",EDGE,{"disambiguationData":[OSD([subQ41]),TDD([makeQuery(id+"F16.opExtrude","CAP_EDGE",EDGE,{"disambiguationData":[OSD([subQ41])],"isStart":false})])],"isStart":false})})])]})]}),makeQuery(id+"F42.opExtrude","SWEPT_FACE",FACE,{"disambiguationData":[OSD([subQ4]),TDD([subQ8])]}),makeQuery(id+"F42.opExtrude","SWEPT_FACE",FACE,{"disambiguationData":[OSD([subQ0]),TDD([subQ2])]})]}),makeQuery(id+"F44.opExtrude","SWEPT_FACE",FACE,{"disambiguationData":[OSD([subQ18]),TDD([subQ21])]}),makeQuery(id+"F44.opExtrude","SWEPT_FACE",FACE,{"disambiguationData":[OSD([subQ15]),TDD([subQ17])]})]}),makeQuery(id+"F46.opExtrude","SWEPT_FACE",FACE,{"disambiguationData":[OSD([subQ24,subQ23,subQ33]),TDD([subQ40])]}),makeQuery(id+"F46.opExtrude","SWEPT_FACE",FACE,{"disambiguationData":[OSD([subQ24,subQ23,subQ22]),TDD([subQ39])]})]}),makeQuery(id+"F48.opExtrude","SWEPT_FACE",FACE,{"disambiguationData":[OSD([subQ24,subQ23,subQ33]),TDD([makeQuery(id+"F46.opExtrude","CAP_EDGE",EDGE,{"disambiguationData":[OSD([subQ24,subQ23,subQ33]),TDD([subQ40])],"isStart":false})])]}),makeQuery(id+"F48.opExtrude","SWEPT_FACE",FACE,{"disambiguationData":[OSD([subQ24,subQ23,subQ22]),TDD([makeQuery(id+"F46.opExtrude","CAP_EDGE",EDGE,{"disambiguationData":[OSD([subQ24,subQ23,subQ22]),TDD([subQ39])],"isStart":false})])]})]}),makeQuery(id+"F50.opExtrude","SWEPT_FACE",FACE,{"disambiguationData":[OSD([subQ4]),TDD([subQ9])]})]}),makeQuery(id+"F51.opExtrude","SWEPT_FACE",FACE,{"disambiguationData":[OSD([subQ0]),TDD([subQ3])]})]}),makeQuery(id+"F53.opExtrude","SWEPT_FACE",FACE,{"disambiguationData":[OSD([subQ18]),TDD([makeQuery(id+"F44.opExtrude","CAP_EDGE",EDGE,{"disambiguationData":[OSD([subQ18]),TDD([subQ21])],"isStart":false})])]}),makeQuery(id+"F53.opExtrude","SWEPT_FACE",FACE,{"disambiguationData":[OSD([subQ15]),TDD([makeQuery(id+"F44.opExtrude","CAP_EDGE",EDGE,{"disambiguationData":[OSD([subQ15]),TDD([subQ17])],"isStart":false})])]})]}),makeQuery(id+"F55.opExtrude","SWEPT_FACE",FACE,{"disambiguationData":[OSD([subQ11]),TDD([makeQuery(id+"F54.boolean.opBoolean","COPY",EDGE,{"derivedFrom":makeQuery(id+"F54.opExtrude","CAP_EDGE",EDGE,{"disambiguationData":[OSD([subQ11]),TDD([makeQuery(id+"F45.boolean.opBoolean","COPY",EDGE,{"derivedFrom":makeQuery(id+"F45.opExtrude","CAP_EDGE",EDGE,{"disambiguationData":[OSD([subQ11]),TDD([makeQuery(id+"F31.opExtrude","CAP_EDGE",EDGE,{"disambiguationData":[OSD([subQ11]),TDD([subQ14])],"isStart":false})])],"isStart":false})})])],"isStart":false})})])]}),makeQuery(id+"F55.opExtrude","SWEPT_FACE",FACE,{"disambiguationData":[OSD([subQ10]),TDD([makeQuery(id+"F54.boolean.opBoolean","COPY",EDGE,{"derivedFrom":makeQuery(id+"F54.opExtrude","CAP_EDGE",EDGE,{"disambiguationData":[OSD([subQ10]),TDD([makeQuery(id+"F45.boolean.opBoolean","COPY",EDGE,{"derivedFrom":makeQuery(id+"F45.opExtrude","CAP_EDGE",EDGE,{"disambiguationData":[OSD([subQ10]),TDD([makeQuery(id+"F37.boolean.opBoolean","COPY",EDGE,{"derivedFrom":makeQuery(id+"F37.opExtrude","CAP_EDGE",EDGE,{"disambiguationData":[OSD([subQ10]),TDD([makeQuery(id+"F16.opExtrude","CAP_EDGE",EDGE,{"disambiguationData":[OSD([subQ10])],"isStart":false})])],"isStart":false})})])],"isStart":false})})])],"isStart":false})})])]})]}),makeQuery(id+"F57.opExtrude","SWEPT_FACE",FACE,{"disambiguationData":[OSD([subQ4]),TDD([makeQuery(id+"F50.opExtrude","CAP_EDGE",EDGE,{"disambiguationData":[OSD([subQ4]),TDD([subQ9])],"isStart":false})])]}),makeQuery(id+"F57.opExtrude","SWEPT_FACE",FACE,{"disambiguationData":[OSD([subQ0]),TDD([makeQuery(id+"F51.opExtrude","CAP_EDGE",EDGE,{"disambiguationData":[OSD([subQ0]),TDD([subQ3])],"isStart":false})])]})]});}
            fillet(context, id + "F59", {"entities" : qUnion([Q0]), "radius" : 3 * mm, "tangentPropagation" : true, "allowEdgeOverflow" : false});
        }
    });
